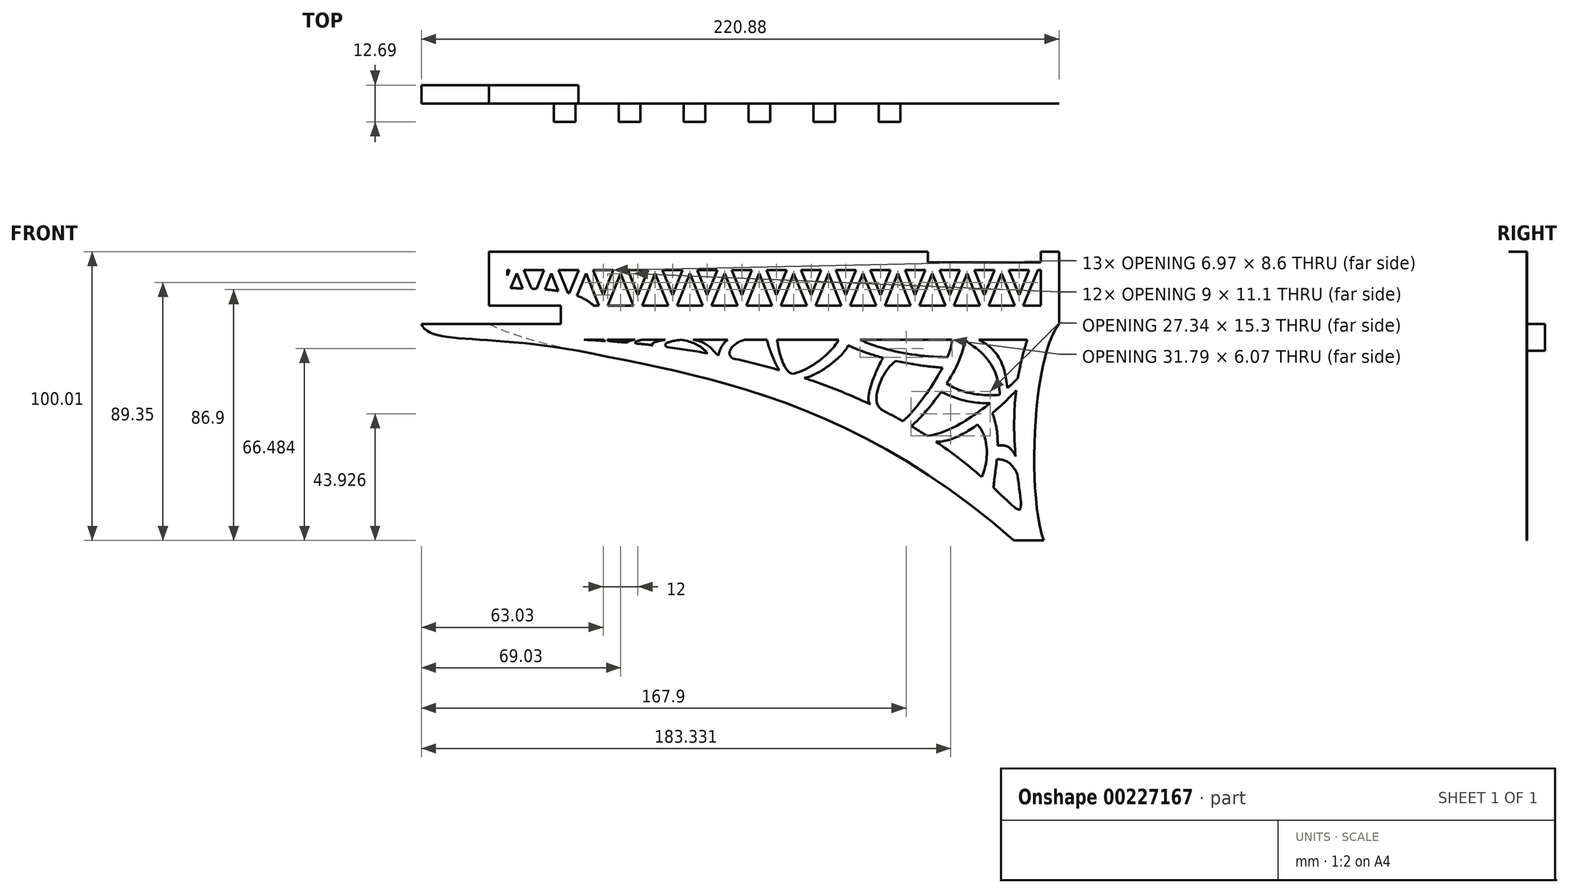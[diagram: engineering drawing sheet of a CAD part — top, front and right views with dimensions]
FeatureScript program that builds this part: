
annotation { "Feature Type Name" : "Feature", "Feature Type Description" : "" }
export const myFeature = defineFeature(function(context is Context, id is Id, definition is map)
    precondition{}
    {
        {
            var Q0;
            Q0=qCreatedBy(makeId("Front.planeOp"),FACE);
            var sketch = newSketch(context, id + "F0", { "sketchPlane" : qUnion([Q0])});
            skLineSegment(sketch, "E0.bottom", {"start": v(98.75, -5) * mm, "end": v(-98.75, -5) * mm});
            skLineSegment(sketch, "E0.top", {"start": v(98.75, 20) * mm, "end": v(-98.75, 20) * mm});
            skLineSegment(sketch, "E0.left", {"start": v(98.75, -5) * mm, "end": v(98.75, 20) * mm});
            skLineSegment(sketch, "E0.right", {"start": v(-98.75, -5) * mm, "end": v(-98.75, 20) * mm});
            skPoint(sketch, "E0.middle", {"position": v(0, 0) * mm});
            skFitSpline(sketch, "E1", {"points": [v(98.75, -5) * mm, v(93.4, -80) * mm], "startDerivative": vector(-27.44, -35.05) * mm, "endDerivative": vector(17.25, -51.42) * mm});
            skLineSegment(sketch, "E2", {"start": v(93.4, -80) * mm, "end": v(83.1, -80) * mm});
            skFitSpline(sketch, "E3", {"points": [v(-98.75, -5) * mm, v(83.1, -80) * mm], "startDerivative": vector(105.32, -51.98) * mm, "endDerivative": vector(225.98, -199.97) * mm});
            skLineSegment(sketch, "E4", {"start": v(-65.76, -10.48) * mm, "end": v(87.75, -10.48) * mm});
            skFitSpline(sketch, "E5", {"points": [v(-65.76, -10.48) * mm, v(85.36, -68.89) * mm, v(87.75, -10.48) * mm], "startDerivative": vector(565.84, -25.35) * mm, "endDerivative": vector(76.27, 228.43) * mm});
            skFitSpline(sketch, "E6", {"points": [v(56.07, -45.75) * mm, v(83.89, -28.03) * mm], "startDerivative": vector(28.17, -2.5) * mm, "endDerivative": vector(10.89, 11.9) * mm});
            skFitSpline(sketch, "E7", {"points": [v(53, -43.72) * mm, v(84.48, -23.78) * mm], "startDerivative": vector(32.82, 2.67) * mm, "endDerivative": vector(17.3, 17.3) * mm});
            skFitSpline(sketch, "E8", {"points": [v(80.84, -27.26) * mm, v(70.98, -10.48) * mm], "startDerivative": vector(-2.04, 19.93) * mm, "endDerivative": vector(-22.58, 10.97) * mm});
            skFitSpline(sketch, "E9", {"points": [v(78.24, -29.58) * mm, v(65.8, -10.48) * mm], "startDerivative": vector(-1.39, 23.06) * mm, "endDerivative": vector(-28.1, 16.92) * mm});
            skFitSpline(sketch, "E10", {"points": [v(65.8, -10.48) * mm, v(47.53, -40.35) * mm], "startDerivative": vector(1.99, -23.82) * mm, "endDerivative": vector(-17.85, -13.78) * mm});
            skFitSpline(sketch, "E11", {"points": [v(44.65, -38.69) * mm, v(61.67, -10.48) * mm], "startDerivative": vector(16.03, 13.18) * mm, "endDerivative": vector(-0.09, 21.32) * mm});
            skFitSpline(sketch, "E12", {"points": [v(60.08, -16.55) * mm, v(29.87, -10.48) * mm], "startDerivative": vector(-38.25, 0.68) * mm, "endDerivative": vector(-20.49, 9.63) * mm});
            skFitSpline(sketch, "E13", {"points": [v(58.36, -20.16) * mm, v(22.4, -10.48) * mm], "startDerivative": vector(-35.97, 2.75) * mm, "endDerivative": vector(-25.01, 16.53) * mm});
            skFitSpline(sketch, "E14", {"points": [v(42.18, -17.79) * mm, v(37.31, -34.77) * mm], "startDerivative": vector(-10.68, -6.67) * mm, "endDerivative": vector(14.47, -11.03) * mm});
            skFitSpline(sketch, "E15", {"points": [v(37.76, -16.72) * mm, v(33.33, -32.82) * mm], "startDerivative": vector(-5.25, -9.39) * mm, "endDerivative": vector(6.74, -7.17) * mm});
            skFitSpline(sketch, "E16", {"points": [v(22.4, -10.48) * mm, v(6.22, -22.3) * mm], "startDerivative": vector(-5.63, -11.87) * mm, "endDerivative": vector(-18.63, -2.94) * mm});
            skFitSpline(sketch, "E17", {"points": [v(25.68, -12.35) * mm, v(10.5, -23.68) * mm], "startDerivative": vector(-3.48, -11.13) * mm, "endDerivative": vector(-14.03, -2) * mm});
            skFitSpline(sketch, "E18", {"points": [v(6.22, -22.3) * mm, v(1.1, -10.48) * mm], "startDerivative": vector(-10.68, 5.46) * mm, "endDerivative": vector(-1.53, 8.83) * mm});
            skFitSpline(sketch, "E19", {"points": [v(-2.49, -10.48) * mm, v(1.88, -21) * mm], "startDerivative": vector(2.88, -9.85) * mm, "endDerivative": vector(4.5, -6.05) * mm});
            skFitSpline(sketch, "E20", {"points": [v(-10.24, -10.48) * mm, v(-14.28, -16.93) * mm], "startDerivative": vector(-13.8, -4.46) * mm, "endDerivative": vector(7.54, -4.85) * mm});
            skFitSpline(sketch, "E21", {"points": [v(-15.96, -10.48) * mm, v(-19.26, -15.9) * mm], "startDerivative": vector(-5.38, -2.77) * mm, "endDerivative": vector(-0.7, -3.9) * mm});
            skFitSpline(sketch, "E22", {"points": [v(-32.12, -10.48) * mm, v(-37.03, -12.98) * mm], "startDerivative": vector(-14.9, -1.57) * mm, "endDerivative": vector(4.86, -2.77) * mm});
            skFitSpline(sketch, "E23", {"points": [v(-37.55, -10.48) * mm, v(-41.88, -12.38) * mm], "startDerivative": vector(-5.93, -0.73) * mm, "endDerivative": vector(4.42, -2.32) * mm});
            skFitSpline(sketch, "E24", {"points": [v(-32.12, -10.48) * mm, v(-23, -15.19) * mm], "startDerivative": vector(17.25, -2.68) * mm, "endDerivative": vector(3.13, -3.72) * mm});
            skFitSpline(sketch, "E25", {"points": [v(-19.26, -15.9) * mm, v(-28.02, -10.48) * mm], "startDerivative": vector(-6.33, 5.02) * mm, "endDerivative": vector(-16.76, 2.48) * mm});
            skFitSpline(sketch, "E26", {"points": [v(-57.31, -10.48) * mm, v(-55.24, -11.1) * mm], "startDerivative": vector(-2.73, -0.64) * mm, "endDerivative": vector(6.17, -0.76) * mm});
            skFitSpline(sketch, "E27", {"points": [v(-58.79, -10.48) * mm, v(-58.33, -10.9) * mm], "startDerivative": vector(-3.78, -0.22) * mm, "endDerivative": vector(1.48, -0.38) * mm});
            skFitSpline(sketch, "E28", {"points": [v(-47.96, -10.48) * mm, v(-50.98, -11.45) * mm], "startDerivative": vector(-5.36, -0.47) * mm, "endDerivative": vector(-1.65, -1.26) * mm});
            skFitSpline(sketch, "E29", {"points": [v(-45.44, -10.48) * mm, v(-47.84, -11.75) * mm], "startDerivative": vector(-6.67, -1.19) * mm, "endDerivative": vector(1.44, -1.22) * mm});
            skFitSpline(sketch, "E30", {"points": [v(70.53, -39.87) * mm, v(71.95, -58) * mm], "startDerivative": vector(13.38, -14.75) * mm, "endDerivative": vector(-6.74, -14.62) * mm});
            skFitSpline(sketch, "E31", {"points": [v(75.63, -35.89) * mm, v(76.05, -61.72) * mm], "startDerivative": vector(10.58, -25.76) * mm, "endDerivative": vector(-2.3, -24.81) * mm});
            skFitSpline(sketch, "E32", {"points": [v(77.51, -47.14) * mm, v(83.68, -50.86) * mm], "startDerivative": vector(10.76, 1.7) * mm, "endDerivative": vector(3.59, -7.85) * mm});
            skFitSpline(sketch, "E33", {"points": [v(77.21, -51.88) * mm, v(84.34, -57.03) * mm], "startDerivative": vector(7.86, 0.06) * mm, "endDerivative": vector(6.37, -13.5) * mm});
            skFitSpline(sketch, "E34", {"points": [v(59.86, -25.57) * mm, v(78.24, -29.58) * mm], "startDerivative": vector(13.5, -9.78) * mm, "endDerivative": vector(20.76, 1.45) * mm});
            skFitSpline(sketch, "E35", {"points": [v(57.95, -28.42) * mm, v(74.87, -32.4) * mm], "startDerivative": vector(12.14, -6.33) * mm, "endDerivative": vector(20.42, 1.15) * mm});
            skLineSegment(sketch, "E36", {"start": v(0, -5) * mm, "end": v(0, 7.5) * mm, "construction": true});
            skLineSegment(sketch, "E37", {"start": v(0, 7.5) * mm, "end": v(0, 20) * mm, "construction": true});
            skLineSegment(sketch, "E38.bottom", {"start": v(92.4, 1.35) * mm, "end": v(-92.4, 1.35) * mm});
            skLineSegment(sketch, "E38.top", {"start": v(92.4, 13.65) * mm, "end": v(-92.4, 13.65) * mm});
            skLineSegment(sketch, "E38.left", {"start": v(92.4, 1.35) * mm, "end": v(92.4, 13.65) * mm});
            skLineSegment(sketch, "E38.right", {"start": v(-92.4, 1.35) * mm, "end": v(-92.4, 13.65) * mm});
            skPoint(sketch, "E38.middle", {"position": v(0, 7.5) * mm});
            skFitSpline(sketch, "E39", {"points": [v(-92.4, 7.35) * mm, v(-62.4, 1.35) * mm], "startDerivative": vector(62.88, 0.86) * mm, "endDerivative": vector(10.76, -9.28) * mm});
            skLineSegment(sketch, "E40", {"start": v(98.75, 16.15) * mm, "end": v(-98.75, 16.15) * mm, "construction": true});
            skLineSegment(sketch, "E41", {"start": v(92.4, 13.65) * mm, "end": v(92.4, 16.15) * mm, "construction": true});
            skLineSegment(sketch, "E42", {"start": v(92.4, 16.15) * mm, "end": v(86.4, 1.35) * mm});
            skLineSegment(sketch, "E43", {"start": v(86.4, 1.35) * mm, "end": v(80.4, 16.15) * mm});
            skLineSegment(sketch, "E44", {"start": v(80.4, 16.15) * mm, "end": v(74.4, 1.35) * mm});
            skLineSegment(sketch, "E45", {"start": v(89.4, 16.15) * mm, "end": v(83.4, 1.35) * mm});
            skLineSegment(sketch, "E46", {"start": v(83.4, 1.35) * mm, "end": v(77.4, 16.15) * mm});
            skLineSegment(sketch, "E47", {"start": v(77.4, 16.15) * mm, "end": v(71.4, 1.35) * mm});
            skLineSegment(sketch, "E48.1.0.0", {"start": v(65.4, 16.15) * mm, "end": v(59.4, 1.35) * mm});
            skLineSegment(sketch, "E48.1.0.1", {"start": v(68.4, 16.15) * mm, "end": v(62.4, 1.35) * mm});
            skLineSegment(sketch, "E48.1.0.2", {"start": v(71.4, 1.35) * mm, "end": v(65.4, 16.15) * mm});
            skLineSegment(sketch, "E48.1.0.3", {"start": v(74.4, 1.35) * mm, "end": v(68.4, 16.15) * mm});
            skLineSegment(sketch, "E48.2.0.0", {"start": v(53.4, 16.15) * mm, "end": v(47.4, 1.35) * mm});
            skLineSegment(sketch, "E48.2.0.1", {"start": v(56.4, 16.15) * mm, "end": v(50.4, 1.35) * mm});
            skLineSegment(sketch, "E48.2.0.2", {"start": v(59.4, 1.35) * mm, "end": v(53.4, 16.15) * mm});
            skLineSegment(sketch, "E48.2.0.3", {"start": v(62.4, 1.35) * mm, "end": v(56.4, 16.15) * mm});
            skLineSegment(sketch, "E48.3.0.0", {"start": v(41.4, 16.15) * mm, "end": v(35.4, 1.35) * mm});
            skLineSegment(sketch, "E48.3.0.1", {"start": v(44.4, 16.15) * mm, "end": v(38.4, 1.35) * mm});
            skLineSegment(sketch, "E48.3.0.2", {"start": v(47.4, 1.35) * mm, "end": v(41.4, 16.15) * mm});
            skLineSegment(sketch, "E48.3.0.3", {"start": v(50.4, 1.35) * mm, "end": v(44.4, 16.15) * mm});
            skLineSegment(sketch, "E48.4.0.0", {"start": v(29.4, 16.15) * mm, "end": v(23.4, 1.35) * mm});
            skLineSegment(sketch, "E48.4.0.1", {"start": v(32.4, 16.15) * mm, "end": v(26.4, 1.35) * mm});
            skLineSegment(sketch, "E48.4.0.2", {"start": v(35.4, 1.35) * mm, "end": v(29.4, 16.15) * mm});
            skLineSegment(sketch, "E48.4.0.3", {"start": v(38.4, 1.35) * mm, "end": v(32.4, 16.15) * mm});
            skLineSegment(sketch, "E48.5.0.0", {"start": v(17.4, 16.15) * mm, "end": v(11.4, 1.35) * mm});
            skLineSegment(sketch, "E48.5.0.1", {"start": v(20.4, 16.15) * mm, "end": v(14.4, 1.35) * mm});
            skLineSegment(sketch, "E48.5.0.2", {"start": v(23.4, 1.35) * mm, "end": v(17.4, 16.15) * mm});
            skLineSegment(sketch, "E48.5.0.3", {"start": v(26.4, 1.35) * mm, "end": v(20.4, 16.15) * mm});
            skLineSegment(sketch, "E48.6.0.0", {"start": v(5.4, 16.15) * mm, "end": v(-0.6, 1.35) * mm});
            skLineSegment(sketch, "E48.6.0.1", {"start": v(8.4, 16.15) * mm, "end": v(2.4, 1.35) * mm});
            skLineSegment(sketch, "E48.6.0.2", {"start": v(11.4, 1.35) * mm, "end": v(5.4, 16.15) * mm});
            skLineSegment(sketch, "E48.6.0.3", {"start": v(14.4, 1.35) * mm, "end": v(8.4, 16.15) * mm});
            skLineSegment(sketch, "E48.7.0.0", {"start": v(-6.6, 16.15) * mm, "end": v(-12.6, 1.35) * mm});
            skLineSegment(sketch, "E48.7.0.1", {"start": v(-3.6, 16.15) * mm, "end": v(-9.6, 1.35) * mm});
            skLineSegment(sketch, "E48.7.0.2", {"start": v(-0.6, 1.35) * mm, "end": v(-6.6, 16.15) * mm});
            skLineSegment(sketch, "E48.7.0.3", {"start": v(2.4, 1.35) * mm, "end": v(-3.6, 16.15) * mm});
            skLineSegment(sketch, "E48.8.0.0", {"start": v(-18.6, 16.15) * mm, "end": v(-24.6, 1.35) * mm});
            skLineSegment(sketch, "E48.8.0.1", {"start": v(-15.6, 16.15) * mm, "end": v(-21.6, 1.35) * mm});
            skLineSegment(sketch, "E48.8.0.2", {"start": v(-12.6, 1.35) * mm, "end": v(-18.6, 16.15) * mm});
            skLineSegment(sketch, "E48.8.0.3", {"start": v(-9.6, 1.35) * mm, "end": v(-15.6, 16.15) * mm});
            skLineSegment(sketch, "E48.9.0.0", {"start": v(-30.6, 16.15) * mm, "end": v(-36.6, 1.35) * mm});
            skLineSegment(sketch, "E48.9.0.1", {"start": v(-27.6, 16.15) * mm, "end": v(-33.6, 1.35) * mm});
            skLineSegment(sketch, "E48.9.0.2", {"start": v(-24.6, 1.35) * mm, "end": v(-30.6, 16.15) * mm});
            skLineSegment(sketch, "E48.9.0.3", {"start": v(-21.6, 1.35) * mm, "end": v(-27.6, 16.15) * mm});
            skLineSegment(sketch, "E48.10.0.0", {"start": v(-42.6, 16.15) * mm, "end": v(-48.6, 1.35) * mm});
            skLineSegment(sketch, "E48.10.0.1", {"start": v(-39.6, 16.15) * mm, "end": v(-45.6, 1.35) * mm});
            skLineSegment(sketch, "E48.10.0.2", {"start": v(-36.6, 1.35) * mm, "end": v(-42.6, 16.15) * mm});
            skLineSegment(sketch, "E48.10.0.3", {"start": v(-33.6, 1.35) * mm, "end": v(-39.6, 16.15) * mm});
            skLineSegment(sketch, "E48.11.0.0", {"start": v(-54.6, 16.15) * mm, "end": v(-60.6, 1.35) * mm});
            skLineSegment(sketch, "E48.11.0.1", {"start": v(-51.6, 16.15) * mm, "end": v(-57.6, 1.35) * mm});
            skLineSegment(sketch, "E48.11.0.2", {"start": v(-48.6, 1.35) * mm, "end": v(-54.6, 16.15) * mm});
            skLineSegment(sketch, "E48.11.0.3", {"start": v(-45.6, 1.35) * mm, "end": v(-51.6, 16.15) * mm});
            skLineSegment(sketch, "E48.12.0.0", {"start": v(-66.6, 16.15) * mm, "end": v(-72.6, 1.35) * mm});
            skLineSegment(sketch, "E48.12.0.1", {"start": v(-63.6, 16.15) * mm, "end": v(-69.6, 1.35) * mm});
            skLineSegment(sketch, "E48.12.0.2", {"start": v(-60.6, 1.35) * mm, "end": v(-66.6, 16.15) * mm});
            skLineSegment(sketch, "E48.12.0.3", {"start": v(-57.6, 1.35) * mm, "end": v(-63.6, 16.15) * mm});
            skLineSegment(sketch, "E48.13.0.0", {"start": v(-78.6, 16.15) * mm, "end": v(-84.6, 1.35) * mm});
            skLineSegment(sketch, "E48.13.0.1", {"start": v(-75.6, 16.15) * mm, "end": v(-81.6, 1.35) * mm});
            skLineSegment(sketch, "E48.13.0.2", {"start": v(-72.6, 1.35) * mm, "end": v(-78.6, 16.15) * mm});
            skLineSegment(sketch, "E48.13.0.3", {"start": v(-69.6, 1.35) * mm, "end": v(-75.6, 16.15) * mm});
            skLineSegment(sketch, "E48.14.0.0", {"start": v(-90.6, 16.15) * mm, "end": v(-96.6, 1.35) * mm});
            skLineSegment(sketch, "E48.14.0.1", {"start": v(-87.6, 16.15) * mm, "end": v(-93.6, 1.35) * mm});
            skLineSegment(sketch, "E48.14.0.2", {"start": v(-84.6, 1.35) * mm, "end": v(-90.6, 16.15) * mm});
            skLineSegment(sketch, "E48.14.0.3", {"start": v(-81.6, 1.35) * mm, "end": v(-87.6, 16.15) * mm});
            skLineSegment(sketch, "E48.direction1", {"start": v(71.4, 1.35) * mm, "end": v(59.4, 1.35) * mm, "construction": true});
            skSolve(sketch);
        }
        {
            var Q0;
            Q0=makeQuery(id+"F0.imprint","IMPRINT",FACE,{"disambiguationData":[TD([[makeQuery(id+"F0.imprint","IMPRINT",EDGE,{"derivedFrom":sQuery(id+"F0.wireOp",EDGE,"E0.bottom")}),1.0]])]});
            var Q1;
            {var subQ0=sQuery(id+"F0.wireOp",EDGE,"E8");Q1=makeQuery(id+"F0.imprint","IMPRINT",FACE,{"disambiguationData":[TD([[makeQuery(id+"F0.imprint","IMPRINT",EDGE,{"derivedFrom":subQ0}),1.0]])]});}
            var Q2;
            {var subQ4=sQuery(id+"F0.wireOp",EDGE,"E6");Q2=makeQuery(id+"F0.imprint","IMPRINT",FACE,{"disambiguationData":[TD([[makeQuery(id+"F0.imprint","IMPRINT",EDGE,{"derivedFrom":subQ4}),1.0]])]});}
            var Q3;
            {var subQ4=sQuery(id+"F0.wireOp",EDGE,"E12");Q3=makeQuery(id+"F0.imprint","IMPRINT",FACE,{"disambiguationData":[TD([[makeQuery(id+"F0.imprint","IMPRINT",EDGE,{"derivedFrom":subQ4}),1.0]])]});}
            var Q4;
            {var subQ4=sQuery(id+"F0.wireOp",EDGE,"E10");Q4=makeQuery(id+"F0.imprint","IMPRINT",FACE,{"disambiguationData":[TD([[makeQuery(id+"F0.imprint","IMPRINT",EDGE,{"derivedFrom":subQ4}),-1.0]])]});}
            var Q5;
            {var subQ0=sQuery(id+"F0.wireOp",EDGE,"E14");Q5=makeQuery(id+"F0.imprint","IMPRINT",FACE,{"disambiguationData":[TD([[makeQuery(id+"F0.imprint","IMPRINT",EDGE,{"derivedFrom":subQ0}),-1.0]])]});}
            var Q6;
            {var subQ0=sQuery(id+"F0.wireOp",EDGE,"E18");Q6=makeQuery(id+"F0.imprint","IMPRINT",FACE,{"disambiguationData":[TD([[makeQuery(id+"F0.imprint","IMPRINT",EDGE,{"derivedFrom":subQ0}),1.0]])]});}
            var Q7;
            {var subQ0=sQuery(id+"F0.wireOp",EDGE,"E20");Q7=makeQuery(id+"F0.imprint","IMPRINT",FACE,{"disambiguationData":[TD([[makeQuery(id+"F0.imprint","IMPRINT",EDGE,{"derivedFrom":subQ0}),-1.0]])]});}
            var Q8;
            {var subQ0=sQuery(id+"F0.wireOp",EDGE,"E16");Q8=makeQuery(id+"F0.imprint","IMPRINT",FACE,{"disambiguationData":[TD([[makeQuery(id+"F0.imprint","IMPRINT",EDGE,{"derivedFrom":subQ0}),1.0]])]});}
            var Q9;
            {var subQ0=sQuery(id+"F0.wireOp",EDGE,"E22");Q9=makeQuery(id+"F0.imprint","IMPRINT",FACE,{"disambiguationData":[TD([[makeQuery(id+"F0.imprint","IMPRINT",EDGE,{"derivedFrom":subQ0}),-1.0]])]});}
            var Q10;
            {var subQ0=sQuery(id+"F0.wireOp",EDGE,"E24");Q10=makeQuery(id+"F0.imprint","IMPRINT",FACE,{"disambiguationData":[TD([[makeQuery(id+"F0.imprint","IMPRINT",EDGE,{"derivedFrom":subQ0}),1.0]])]});}
            var Q11;
            {var subQ3=sQuery(id+"F0.wireOp",EDGE,"E26");Q11=makeQuery(id+"F0.imprint","IMPRINT",FACE,{"disambiguationData":[TD([[makeQuery(id+"F0.imprint","IMPRINT",EDGE,{"derivedFrom":subQ3}),-1.0]])]});}
            var Q12;
            {var subQ0=sQuery(id+"F0.wireOp",EDGE,"E28");Q12=makeQuery(id+"F0.imprint","IMPRINT",FACE,{"disambiguationData":[TD([[makeQuery(id+"F0.imprint","IMPRINT",EDGE,{"derivedFrom":subQ0}),1.0]])]});}
            var Q13;
            {var subQ0=sQuery(id+"F0.wireOp",EDGE,"0f1a2a49-f85b-4a7b-b702-23d574d83e41");Q13=makeQuery(id+"F0.imprint","IMPRINT",FACE,{"disambiguationData":[TD([[makeQuery(id+"F0.imprint","IMPRINT",EDGE,{"derivedFrom":subQ0}),-1.0]])]});}
            var Q14;
            {var subQ0=sQuery(id+"F0.wireOp",EDGE,"ffe359e4-6994-4db7-aa5d-63739de77c5f");Q14=makeQuery(id+"F0.imprint","IMPRINT",FACE,{"disambiguationData":[TD([[makeQuery(id+"F0.imprint","IMPRINT",EDGE,{"derivedFrom":subQ0}),-1.0]])]});}
            var Q15;
            {var subQ4=sQuery(id+"F0.wireOp",EDGE,"E30");Q15=makeQuery(id+"F0.imprint","IMPRINT",FACE,{"disambiguationData":[TD([[makeQuery(id+"F0.imprint","IMPRINT",EDGE,{"derivedFrom":subQ4}),1.0]])]});}
            var Q16;
            {var subQ0=sQuery(id+"F0.wireOp",EDGE,"E32");Q16=makeQuery(id+"F0.imprint","IMPRINT",FACE,{"disambiguationData":[TD([[makeQuery(id+"F0.imprint","IMPRINT",EDGE,{"derivedFrom":subQ0}),-1.0]])]});}
            var Q17;
            {var subQ0=sQuery(id+"F0.wireOp",EDGE,"E34");Q17=makeQuery(id+"F0.imprint","IMPRINT",FACE,{"disambiguationData":[TD([[makeQuery(id+"F0.imprint","IMPRINT",EDGE,{"derivedFrom":subQ0}),-1.0]])]});}
            var Q18;
            {var subQ0=sQuery(id+"F0.wireOp",EDGE,"GfOTP1Av-60BQ-FTfT-Dyfk-SZfRFgkm87CM");Q18=makeQuery(id+"F0.imprint","IMPRINT",FACE,{"disambiguationData":[TD([[makeQuery(id+"F0.imprint","IMPRINT",EDGE,{"derivedFrom":subQ0}),1.0]])]});}
            var Q19;
            {var subQ3=sQuery(id+"F0.wireOp",EDGE,"E39");Q19=makeQuery(id+"F0.imprint","IMPRINT",FACE,{"disambiguationData":[TD([[makeQuery(id+"F0.imprint","IMPRINT",EDGE,{"derivedFrom":subQ3}),-1.0]])]});}
            var Q20;
            {var subQ0=sQuery(id+"F0.wireOp",EDGE,"6nG8yHqI-1RSW-Lih2-RL7p-Ogt5qLZxJ40G");Q20=makeQuery(id+"F0.imprint","IMPRINT",FACE,{"disambiguationData":[TD([[makeQuery(id+"F0.imprint","IMPRINT",EDGE,{"derivedFrom":subQ0}),-1.0]])]});}
            var Q21;
            {var subQ0=sQuery(id+"F0.wireOp",EDGE,"vsQBDWpD-XZvz-YL4w-sYMF-8ExcL3MSyagj");var subQ3=sQuery(id+"F0.wireOp",EDGE,"ahGiBcFi-U1tk-ofgL-IaMi-E3z2y5cFStP9");var subQ5=makeQuery(id+"F0.imprint","INTERSECT",VERTEX,{"derivedFrom":[subQ0,subQ3]});Q21=makeQuery(id+"F0.imprint","IMPRINT",FACE,{"disambiguationData":[TD([[makeQuery(id+"F0.imprint","IMPRINT",EDGE,{"disambiguationData":[TD([[subQ5,-1.0]])],"derivedFrom":subQ0}),1.0]])]});}
            var Q22;
            {var subQ0=sQuery(id+"F0.wireOp",EDGE,"E46");var subQ1=sQuery(id+"F0.wireOp",EDGE,"E38.top");var subQ2=makeQuery(id+"F0.imprint","INTERSECT",VERTEX,{"derivedFrom":[subQ1,subQ0]});Q22=makeQuery(id+"F0.imprint","IMPRINT",FACE,{"disambiguationData":[TD([[makeQuery(id+"F0.imprint","IMPRINT",EDGE,{"disambiguationData":[TD([[subQ2,-1.0]])],"derivedFrom":subQ1}),-1.0]])]});}
            var Q23;
            {var subQ0=sQuery(id+"F0.wireOp",EDGE,"E43");var subQ1=sQuery(id+"F0.wireOp",EDGE,"E38.top");var subQ2=makeQuery(id+"F0.imprint","INTERSECT",VERTEX,{"derivedFrom":[subQ1,subQ0]});Q23=makeQuery(id+"F0.imprint","IMPRINT",FACE,{"disambiguationData":[TD([[makeQuery(id+"F0.imprint","IMPRINT",EDGE,{"disambiguationData":[TD([[subQ2,-1.0]])],"derivedFrom":subQ1}),-1.0]])]});}
            var Q24;
            {var subQ1=sQuery(id+"F0.wireOp",EDGE,"E38.right");var subQ7=sQuery(id+"F0.wireOp",EDGE,"E38.bottom");var subQ8=makeQuery(id+"F0.imprint","INTERSECT",VERTEX,{"derivedFrom":[subQ7,subQ1]});Q24=makeQuery(id+"F0.imprint","IMPRINT",FACE,{"disambiguationData":[TD([[makeQuery(id+"F0.imprint","IMPRINT",EDGE,{"disambiguationData":[TD([[subQ8,-1.0]])],"derivedFrom":subQ1}),-1.0]])]});}
            var Q25;
            {var subQ0=sQuery(id+"F0.wireOp",EDGE,"E48.14.0.2");var subQ1=sQuery(id+"F0.wireOp",EDGE,"E39");var subQ2=makeQuery(id+"F0.imprint","INTERSECT",VERTEX,{"derivedFrom":[subQ1,subQ0]});Q25=makeQuery(id+"F0.imprint","IMPRINT",FACE,{"disambiguationData":[TD([[makeQuery(id+"F0.imprint","IMPRINT",EDGE,{"disambiguationData":[TD([[subQ2,-1.0]])],"derivedFrom":subQ1}),-1.0]])]});}
            var Q26;
            {var subQ0=sQuery(id+"F0.wireOp",EDGE,"E48.13.0.0");var subQ3=sQuery(id+"F0.wireOp",EDGE,"E48.14.0.3");var subQ5=makeQuery(id+"F0.imprint","INTERSECT",VERTEX,{"derivedFrom":[subQ0,subQ3]});Q26=makeQuery(id+"F0.imprint","IMPRINT",FACE,{"disambiguationData":[TD([[makeQuery(id+"F0.imprint","IMPRINT",EDGE,{"disambiguationData":[TD([[subQ5,-1.0]])],"derivedFrom":subQ0}),1.0]])]});}
            var Q27;
            {var subQ0=sQuery(id+"F0.wireOp",EDGE,"E48.13.0.0");var subQ1=sQuery(id+"F0.wireOp",EDGE,"E39");var subQ2=makeQuery(id+"F0.imprint","INTERSECT",VERTEX,{"derivedFrom":[subQ1,subQ0]});Q27=makeQuery(id+"F0.imprint","IMPRINT",FACE,{"disambiguationData":[TD([[makeQuery(id+"F0.imprint","IMPRINT",EDGE,{"disambiguationData":[TD([[subQ2,-1.0]])],"derivedFrom":subQ1}),-1.0]])]});}
            var Q28;
            {var subQ3=sQuery(id+"F0.wireOp",EDGE,"E48.13.0.1");var subQ5=sQuery(id+"F0.wireOp",EDGE,"E39");var subQ6=makeQuery(id+"F0.imprint","INTERSECT",VERTEX,{"derivedFrom":[subQ5,subQ3]});Q28=makeQuery(id+"F0.imprint","IMPRINT",FACE,{"disambiguationData":[TD([[makeQuery(id+"F0.imprint","IMPRINT",EDGE,{"disambiguationData":[TD([[subQ6,-1.0]])],"derivedFrom":subQ5}),-1.0]])]});}
            var Q29;
            {var subQ0=sQuery(id+"F0.wireOp",EDGE,"E48.13.0.2");var subQ1=sQuery(id+"F0.wireOp",EDGE,"E39");var subQ2=makeQuery(id+"F0.imprint","INTERSECT",VERTEX,{"derivedFrom":[subQ1,subQ0]});Q29=makeQuery(id+"F0.imprint","IMPRINT",FACE,{"disambiguationData":[TD([[makeQuery(id+"F0.imprint","IMPRINT",EDGE,{"disambiguationData":[TD([[subQ2,-1.0]])],"derivedFrom":subQ1}),-1.0]])]});}
            var Q30;
            {var subQ0=sQuery(id+"F0.wireOp",EDGE,"E48.12.0.0");var subQ3=sQuery(id+"F0.wireOp",EDGE,"E48.13.0.3");var subQ5=makeQuery(id+"F0.imprint","INTERSECT",VERTEX,{"derivedFrom":[subQ0,subQ3]});Q30=makeQuery(id+"F0.imprint","IMPRINT",FACE,{"disambiguationData":[TD([[makeQuery(id+"F0.imprint","IMPRINT",EDGE,{"disambiguationData":[TD([[subQ5,-1.0]])],"derivedFrom":subQ0}),1.0]])]});}
            var Q31;
            {var subQ0=sQuery(id+"F0.wireOp",EDGE,"E48.12.0.0");var subQ1=sQuery(id+"F0.wireOp",EDGE,"E39");var subQ2=makeQuery(id+"F0.imprint","INTERSECT",VERTEX,{"derivedFrom":[subQ1,subQ0]});Q31=makeQuery(id+"F0.imprint","IMPRINT",FACE,{"disambiguationData":[TD([[makeQuery(id+"F0.imprint","IMPRINT",EDGE,{"disambiguationData":[TD([[subQ2,-1.0]])],"derivedFrom":subQ1}),-1.0]])]});}
            var Q32;
            {var subQ0=sQuery(id+"F0.wireOp",EDGE,"E48.14.0.3");var subQ1=sQuery(id+"F0.wireOp",EDGE,"E38.top");var subQ2=makeQuery(id+"F0.imprint","INTERSECT",VERTEX,{"derivedFrom":[subQ1,subQ0]});Q32=makeQuery(id+"F0.imprint","IMPRINT",FACE,{"disambiguationData":[TD([[makeQuery(id+"F0.imprint","IMPRINT",EDGE,{"disambiguationData":[TD([[subQ2,-1.0]])],"derivedFrom":subQ1}),-1.0]])]});}
            var Q33;
            {var subQ0=sQuery(id+"F0.wireOp",EDGE,"E48.14.0.2");var subQ1=sQuery(id+"F0.wireOp",EDGE,"E38.top");var subQ2=makeQuery(id+"F0.imprint","INTERSECT",VERTEX,{"derivedFrom":[subQ1,subQ0]});Q33=makeQuery(id+"F0.imprint","IMPRINT",FACE,{"disambiguationData":[TD([[makeQuery(id+"F0.imprint","IMPRINT",EDGE,{"disambiguationData":[TD([[subQ2,-1.0]])],"derivedFrom":subQ1}),-1.0]])]});}
            var Q34;
            {var subQ0=sQuery(id+"F0.wireOp",EDGE,"E48.13.0.2");var subQ1=sQuery(id+"F0.wireOp",EDGE,"E38.top");var subQ2=makeQuery(id+"F0.imprint","INTERSECT",VERTEX,{"derivedFrom":[subQ1,subQ0]});Q34=makeQuery(id+"F0.imprint","IMPRINT",FACE,{"disambiguationData":[TD([[makeQuery(id+"F0.imprint","IMPRINT",EDGE,{"disambiguationData":[TD([[subQ2,-1.0]])],"derivedFrom":subQ1}),-1.0]])]});}
            var Q35;
            {var subQ0=sQuery(id+"F0.wireOp",EDGE,"E48.13.0.3");var subQ1=sQuery(id+"F0.wireOp",EDGE,"E38.top");var subQ2=makeQuery(id+"F0.imprint","INTERSECT",VERTEX,{"derivedFrom":[subQ1,subQ0]});Q35=makeQuery(id+"F0.imprint","IMPRINT",FACE,{"disambiguationData":[TD([[makeQuery(id+"F0.imprint","IMPRINT",EDGE,{"disambiguationData":[TD([[subQ2,-1.0]])],"derivedFrom":subQ1}),-1.0]])]});}
            var Q36;
            {var subQ0=sQuery(id+"F0.wireOp",EDGE,"E48.12.0.2");var subQ1=sQuery(id+"F0.wireOp",EDGE,"E38.top");var subQ2=makeQuery(id+"F0.imprint","INTERSECT",VERTEX,{"derivedFrom":[subQ1,subQ0]});Q36=makeQuery(id+"F0.imprint","IMPRINT",FACE,{"disambiguationData":[TD([[makeQuery(id+"F0.imprint","IMPRINT",EDGE,{"disambiguationData":[TD([[subQ2,-1.0]])],"derivedFrom":subQ1}),-1.0]])]});}
            var Q37;
            {var subQ0=sQuery(id+"F0.wireOp",EDGE,"E48.12.0.3");var subQ1=sQuery(id+"F0.wireOp",EDGE,"E38.top");var subQ2=makeQuery(id+"F0.imprint","INTERSECT",VERTEX,{"derivedFrom":[subQ1,subQ0]});Q37=makeQuery(id+"F0.imprint","IMPRINT",FACE,{"disambiguationData":[TD([[makeQuery(id+"F0.imprint","IMPRINT",EDGE,{"disambiguationData":[TD([[subQ2,-1.0]])],"derivedFrom":subQ1}),-1.0]])]});}
            var Q38;
            {var subQ0=sQuery(id+"F0.wireOp",EDGE,"E48.11.0.2");var subQ1=sQuery(id+"F0.wireOp",EDGE,"E38.top");var subQ2=makeQuery(id+"F0.imprint","INTERSECT",VERTEX,{"derivedFrom":[subQ1,subQ0]});Q38=makeQuery(id+"F0.imprint","IMPRINT",FACE,{"disambiguationData":[TD([[makeQuery(id+"F0.imprint","IMPRINT",EDGE,{"disambiguationData":[TD([[subQ2,-1.0]])],"derivedFrom":subQ1}),-1.0]])]});}
            var Q39;
            {var subQ0=sQuery(id+"F0.wireOp",EDGE,"E48.11.0.3");var subQ1=sQuery(id+"F0.wireOp",EDGE,"E38.top");var subQ2=makeQuery(id+"F0.imprint","INTERSECT",VERTEX,{"derivedFrom":[subQ1,subQ0]});Q39=makeQuery(id+"F0.imprint","IMPRINT",FACE,{"disambiguationData":[TD([[makeQuery(id+"F0.imprint","IMPRINT",EDGE,{"disambiguationData":[TD([[subQ2,-1.0]])],"derivedFrom":subQ1}),-1.0]])]});}
            var Q40;
            {var subQ0=sQuery(id+"F0.wireOp",EDGE,"E48.10.0.2");var subQ1=sQuery(id+"F0.wireOp",EDGE,"E38.top");var subQ2=makeQuery(id+"F0.imprint","INTERSECT",VERTEX,{"derivedFrom":[subQ1,subQ0]});Q40=makeQuery(id+"F0.imprint","IMPRINT",FACE,{"disambiguationData":[TD([[makeQuery(id+"F0.imprint","IMPRINT",EDGE,{"disambiguationData":[TD([[subQ2,-1.0]])],"derivedFrom":subQ1}),-1.0]])]});}
            var Q41;
            {var subQ0=sQuery(id+"F0.wireOp",EDGE,"E48.10.0.3");var subQ1=sQuery(id+"F0.wireOp",EDGE,"E38.top");var subQ2=makeQuery(id+"F0.imprint","INTERSECT",VERTEX,{"derivedFrom":[subQ1,subQ0]});Q41=makeQuery(id+"F0.imprint","IMPRINT",FACE,{"disambiguationData":[TD([[makeQuery(id+"F0.imprint","IMPRINT",EDGE,{"disambiguationData":[TD([[subQ2,-1.0]])],"derivedFrom":subQ1}),-1.0]])]});}
            var Q42;
            {var subQ0=sQuery(id+"F0.wireOp",EDGE,"E48.9.0.2");var subQ1=sQuery(id+"F0.wireOp",EDGE,"E38.top");var subQ2=makeQuery(id+"F0.imprint","INTERSECT",VERTEX,{"derivedFrom":[subQ1,subQ0]});Q42=makeQuery(id+"F0.imprint","IMPRINT",FACE,{"disambiguationData":[TD([[makeQuery(id+"F0.imprint","IMPRINT",EDGE,{"disambiguationData":[TD([[subQ2,-1.0]])],"derivedFrom":subQ1}),-1.0]])]});}
            var Q43;
            {var subQ0=sQuery(id+"F0.wireOp",EDGE,"E48.9.0.3");var subQ1=sQuery(id+"F0.wireOp",EDGE,"E38.top");var subQ2=makeQuery(id+"F0.imprint","INTERSECT",VERTEX,{"derivedFrom":[subQ1,subQ0]});Q43=makeQuery(id+"F0.imprint","IMPRINT",FACE,{"disambiguationData":[TD([[makeQuery(id+"F0.imprint","IMPRINT",EDGE,{"disambiguationData":[TD([[subQ2,-1.0]])],"derivedFrom":subQ1}),-1.0]])]});}
            var Q44;
            {var subQ0=sQuery(id+"F0.wireOp",EDGE,"E48.8.0.2");var subQ1=sQuery(id+"F0.wireOp",EDGE,"E38.top");var subQ2=makeQuery(id+"F0.imprint","INTERSECT",VERTEX,{"derivedFrom":[subQ1,subQ0]});Q44=makeQuery(id+"F0.imprint","IMPRINT",FACE,{"disambiguationData":[TD([[makeQuery(id+"F0.imprint","IMPRINT",EDGE,{"disambiguationData":[TD([[subQ2,-1.0]])],"derivedFrom":subQ1}),-1.0]])]});}
            var Q45;
            {var subQ0=sQuery(id+"F0.wireOp",EDGE,"E48.8.0.3");var subQ1=sQuery(id+"F0.wireOp",EDGE,"E38.top");var subQ2=makeQuery(id+"F0.imprint","INTERSECT",VERTEX,{"derivedFrom":[subQ1,subQ0]});Q45=makeQuery(id+"F0.imprint","IMPRINT",FACE,{"disambiguationData":[TD([[makeQuery(id+"F0.imprint","IMPRINT",EDGE,{"disambiguationData":[TD([[subQ2,-1.0]])],"derivedFrom":subQ1}),-1.0]])]});}
            var Q46;
            {var subQ0=sQuery(id+"F0.wireOp",EDGE,"E48.7.0.2");var subQ1=sQuery(id+"F0.wireOp",EDGE,"E38.top");var subQ2=makeQuery(id+"F0.imprint","INTERSECT",VERTEX,{"derivedFrom":[subQ1,subQ0]});Q46=makeQuery(id+"F0.imprint","IMPRINT",FACE,{"disambiguationData":[TD([[makeQuery(id+"F0.imprint","IMPRINT",EDGE,{"disambiguationData":[TD([[subQ2,-1.0]])],"derivedFrom":subQ1}),-1.0]])]});}
            var Q47;
            {var subQ0=sQuery(id+"F0.wireOp",EDGE,"E48.7.0.3");var subQ1=sQuery(id+"F0.wireOp",EDGE,"E38.top");var subQ2=makeQuery(id+"F0.imprint","INTERSECT",VERTEX,{"derivedFrom":[subQ1,subQ0]});Q47=makeQuery(id+"F0.imprint","IMPRINT",FACE,{"disambiguationData":[TD([[makeQuery(id+"F0.imprint","IMPRINT",EDGE,{"disambiguationData":[TD([[subQ2,-1.0]])],"derivedFrom":subQ1}),-1.0]])]});}
            var Q48;
            {var subQ0=sQuery(id+"F0.wireOp",EDGE,"E48.6.0.2");var subQ1=sQuery(id+"F0.wireOp",EDGE,"E38.top");var subQ2=makeQuery(id+"F0.imprint","INTERSECT",VERTEX,{"derivedFrom":[subQ1,subQ0]});Q48=makeQuery(id+"F0.imprint","IMPRINT",FACE,{"disambiguationData":[TD([[makeQuery(id+"F0.imprint","IMPRINT",EDGE,{"disambiguationData":[TD([[subQ2,-1.0]])],"derivedFrom":subQ1}),-1.0]])]});}
            var Q49;
            {var subQ0=sQuery(id+"F0.wireOp",EDGE,"E48.6.0.3");var subQ1=sQuery(id+"F0.wireOp",EDGE,"E38.top");var subQ2=makeQuery(id+"F0.imprint","INTERSECT",VERTEX,{"derivedFrom":[subQ1,subQ0]});Q49=makeQuery(id+"F0.imprint","IMPRINT",FACE,{"disambiguationData":[TD([[makeQuery(id+"F0.imprint","IMPRINT",EDGE,{"disambiguationData":[TD([[subQ2,-1.0]])],"derivedFrom":subQ1}),-1.0]])]});}
            var Q50;
            {var subQ0=sQuery(id+"F0.wireOp",EDGE,"E48.5.0.2");var subQ1=sQuery(id+"F0.wireOp",EDGE,"E38.top");var subQ2=makeQuery(id+"F0.imprint","INTERSECT",VERTEX,{"derivedFrom":[subQ1,subQ0]});Q50=makeQuery(id+"F0.imprint","IMPRINT",FACE,{"disambiguationData":[TD([[makeQuery(id+"F0.imprint","IMPRINT",EDGE,{"disambiguationData":[TD([[subQ2,-1.0]])],"derivedFrom":subQ1}),-1.0]])]});}
            var Q51;
            Q51=makeQuery(id+"F0.imprint","IMPRINT",FACE,{"disambiguationData":[TD([[makeQuery(id+"F0.imprint","IMPRINT",EDGE,{"derivedFrom":sQuery(id+"F0.wireOp",EDGE,"E0.bottom")}),-1.0]])]});
            var Q52;
            {var subQ0=sQuery(id+"F0.wireOp",EDGE,"E48.5.0.3");var subQ1=sQuery(id+"F0.wireOp",EDGE,"E38.top");var subQ2=makeQuery(id+"F0.imprint","INTERSECT",VERTEX,{"derivedFrom":[subQ1,subQ0]});Q52=makeQuery(id+"F0.imprint","IMPRINT",FACE,{"disambiguationData":[TD([[makeQuery(id+"F0.imprint","IMPRINT",EDGE,{"disambiguationData":[TD([[subQ2,-1.0]])],"derivedFrom":subQ1}),-1.0]])]});}
            var Q53;
            {var subQ0=sQuery(id+"F0.wireOp",EDGE,"E48.4.0.2");var subQ1=sQuery(id+"F0.wireOp",EDGE,"E38.top");var subQ2=makeQuery(id+"F0.imprint","INTERSECT",VERTEX,{"derivedFrom":[subQ1,subQ0]});Q53=makeQuery(id+"F0.imprint","IMPRINT",FACE,{"disambiguationData":[TD([[makeQuery(id+"F0.imprint","IMPRINT",EDGE,{"disambiguationData":[TD([[subQ2,-1.0]])],"derivedFrom":subQ1}),-1.0]])]});}
            var Q54;
            {var subQ0=sQuery(id+"F0.wireOp",EDGE,"E48.4.0.3");var subQ1=sQuery(id+"F0.wireOp",EDGE,"E38.top");var subQ2=makeQuery(id+"F0.imprint","INTERSECT",VERTEX,{"derivedFrom":[subQ1,subQ0]});Q54=makeQuery(id+"F0.imprint","IMPRINT",FACE,{"disambiguationData":[TD([[makeQuery(id+"F0.imprint","IMPRINT",EDGE,{"disambiguationData":[TD([[subQ2,-1.0]])],"derivedFrom":subQ1}),-1.0]])]});}
            var Q55;
            {var subQ0=sQuery(id+"F0.wireOp",EDGE,"E48.3.0.2");var subQ1=sQuery(id+"F0.wireOp",EDGE,"E38.top");var subQ2=makeQuery(id+"F0.imprint","INTERSECT",VERTEX,{"derivedFrom":[subQ1,subQ0]});Q55=makeQuery(id+"F0.imprint","IMPRINT",FACE,{"disambiguationData":[TD([[makeQuery(id+"F0.imprint","IMPRINT",EDGE,{"disambiguationData":[TD([[subQ2,-1.0]])],"derivedFrom":subQ1}),-1.0]])]});}
            var Q56;
            {var subQ0=sQuery(id+"F0.wireOp",EDGE,"E48.3.0.3");var subQ1=sQuery(id+"F0.wireOp",EDGE,"E38.top");var subQ2=makeQuery(id+"F0.imprint","INTERSECT",VERTEX,{"derivedFrom":[subQ1,subQ0]});Q56=makeQuery(id+"F0.imprint","IMPRINT",FACE,{"disambiguationData":[TD([[makeQuery(id+"F0.imprint","IMPRINT",EDGE,{"disambiguationData":[TD([[subQ2,-1.0]])],"derivedFrom":subQ1}),-1.0]])]});}
            var Q57;
            {var subQ0=sQuery(id+"F0.wireOp",EDGE,"E48.2.0.2");var subQ1=sQuery(id+"F0.wireOp",EDGE,"E38.top");var subQ2=makeQuery(id+"F0.imprint","INTERSECT",VERTEX,{"derivedFrom":[subQ1,subQ0]});Q57=makeQuery(id+"F0.imprint","IMPRINT",FACE,{"disambiguationData":[TD([[makeQuery(id+"F0.imprint","IMPRINT",EDGE,{"disambiguationData":[TD([[subQ2,-1.0]])],"derivedFrom":subQ1}),-1.0]])]});}
            var Q58;
            {var subQ0=sQuery(id+"F0.wireOp",EDGE,"E48.2.0.3");var subQ1=sQuery(id+"F0.wireOp",EDGE,"E38.top");var subQ2=makeQuery(id+"F0.imprint","INTERSECT",VERTEX,{"derivedFrom":[subQ1,subQ0]});Q58=makeQuery(id+"F0.imprint","IMPRINT",FACE,{"disambiguationData":[TD([[makeQuery(id+"F0.imprint","IMPRINT",EDGE,{"disambiguationData":[TD([[subQ2,-1.0]])],"derivedFrom":subQ1}),-1.0]])]});}
            var Q59;
            {var subQ0=sQuery(id+"F0.wireOp",EDGE,"E48.1.0.2");var subQ1=sQuery(id+"F0.wireOp",EDGE,"E38.top");var subQ2=makeQuery(id+"F0.imprint","INTERSECT",VERTEX,{"derivedFrom":[subQ1,subQ0]});Q59=makeQuery(id+"F0.imprint","IMPRINT",FACE,{"disambiguationData":[TD([[makeQuery(id+"F0.imprint","IMPRINT",EDGE,{"disambiguationData":[TD([[subQ2,-1.0]])],"derivedFrom":subQ1}),-1.0]])]});}
            var Q60;
            {var subQ0=sQuery(id+"F0.wireOp",EDGE,"E48.1.0.3");var subQ1=sQuery(id+"F0.wireOp",EDGE,"E38.top");var subQ2=makeQuery(id+"F0.imprint","INTERSECT",VERTEX,{"derivedFrom":[subQ1,subQ0]});Q60=makeQuery(id+"F0.imprint","IMPRINT",FACE,{"disambiguationData":[TD([[makeQuery(id+"F0.imprint","IMPRINT",EDGE,{"disambiguationData":[TD([[subQ2,-1.0]])],"derivedFrom":subQ1}),-1.0]])]});}
            extrude(context, id + "F1", {"entities" : qUnion([Q0, Q1, Q2, Q3, Q4, Q5, Q6, Q7, Q8, Q9, Q10, Q11, Q12, Q13, Q14, Q15, Q16, Q17, Q18, Q19, Q20, Q21, Q22, Q23, Q24, Q25, Q26, Q27, Q28, Q29, Q30, Q31, Q32, Q33, Q34, Q35, Q36, Q37, Q38, Q39, Q40, Q41, Q42, Q43, Q44, Q45, Q46, Q47, Q48, Q49, Q50, Q51, Q52, Q53, Q54, Q55, Q56, Q57, Q58, Q59, Q60]), "depth" : 1 / 101.6 * mm});
        }
        {
            var Q0;
            Q0=makeQuery(id+"F1.opExtrude","SWEPT_FACE",FACE,{"disambiguationData":[OSD([sQuery(id+"F0.wireOp",EDGE,"E0.top")])]});
            var sketch = newSketch(context, id + "F2", { "sketchPlane" : qUnion([Q0])});
            skLineSegment(sketch, "E49.bottom", {"start": v(-98.75, 0) * mm, "end": v(-91.25, 0) * mm});
            skLineSegment(sketch, "E49.top", {"start": v(-98.75, -6.35) * mm, "end": v(-91.25, -6.35) * mm});
            skLineSegment(sketch, "E49.left", {"start": v(-98.75, 0) * mm, "end": v(-98.75, -6.35) * mm});
            skLineSegment(sketch, "E49.right", {"start": v(-91.25, 0) * mm, "end": v(-91.25, -6.35) * mm});
            skLineSegment(sketch, "E50.1.0.0", {"start": v(-68.75, 0) * mm, "end": v(-68.75, -6.35) * mm});
            skLineSegment(sketch, "E50.1.0.1", {"start": v(-76.25, 0) * mm, "end": v(-68.75, 0) * mm});
            skLineSegment(sketch, "E50.1.0.2", {"start": v(-76.25, 0) * mm, "end": v(-76.25, -6.35) * mm});
            skLineSegment(sketch, "E50.1.0.3", {"start": v(-76.25, -6.35) * mm, "end": v(-68.75, -6.35) * mm});
            skLineSegment(sketch, "E50.2.0.0", {"start": v(-46.25, 0) * mm, "end": v(-46.25, -6.35) * mm});
            skLineSegment(sketch, "E50.2.0.1", {"start": v(-53.75, 0) * mm, "end": v(-46.25, 0) * mm});
            skLineSegment(sketch, "E50.2.0.2", {"start": v(-53.75, 0) * mm, "end": v(-53.75, -6.35) * mm});
            skLineSegment(sketch, "E50.2.0.3", {"start": v(-53.75, -6.35) * mm, "end": v(-46.25, -6.35) * mm});
            skLineSegment(sketch, "E50.3.0.0", {"start": v(-23.75, 0) * mm, "end": v(-23.75, -6.35) * mm});
            skLineSegment(sketch, "E50.3.0.1", {"start": v(-31.25, 0) * mm, "end": v(-23.75, 0) * mm});
            skLineSegment(sketch, "E50.3.0.2", {"start": v(-31.25, 0) * mm, "end": v(-31.25, -6.35) * mm});
            skLineSegment(sketch, "E50.3.0.3", {"start": v(-31.25, -6.35) * mm, "end": v(-23.75, -6.35) * mm});
            skLineSegment(sketch, "E50.4.0.0", {"start": v(-1.25, 0) * mm, "end": v(-1.25, -6.35) * mm});
            skLineSegment(sketch, "E50.4.0.1", {"start": v(-8.75, 0) * mm, "end": v(-1.25, 0) * mm});
            skLineSegment(sketch, "E50.4.0.2", {"start": v(-8.75, 0) * mm, "end": v(-8.75, -6.35) * mm});
            skLineSegment(sketch, "E50.4.0.3", {"start": v(-8.75, -6.35) * mm, "end": v(-1.25, -6.35) * mm});
            skLineSegment(sketch, "E50.5.0.0", {"start": v(21.25, 0) * mm, "end": v(21.25, -6.35) * mm});
            skLineSegment(sketch, "E50.5.0.1", {"start": v(13.75, 0) * mm, "end": v(21.25, 0) * mm});
            skLineSegment(sketch, "E50.5.0.2", {"start": v(13.75, 0) * mm, "end": v(13.75, -6.35) * mm});
            skLineSegment(sketch, "E50.5.0.3", {"start": v(13.75, -6.35) * mm, "end": v(21.25, -6.35) * mm});
            skLineSegment(sketch, "E50.6.0.0", {"start": v(43.75, 0) * mm, "end": v(43.75, -6.35) * mm});
            skLineSegment(sketch, "E50.6.0.1", {"start": v(36.25, 0) * mm, "end": v(43.75, 0) * mm});
            skLineSegment(sketch, "E50.6.0.2", {"start": v(36.25, 0) * mm, "end": v(36.25, -6.35) * mm});
            skLineSegment(sketch, "E50.6.0.3", {"start": v(36.25, -6.35) * mm, "end": v(43.75, -6.35) * mm});
            skLineSegment(sketch, "E50.direction1", {"start": v(-91.25, -6.35) * mm, "end": v(-68.75, -6.35) * mm, "construction": true});
            skSolve(sketch);
        }
        {
            var Q0;
            Q0=makeQuery(id+"F2.imprint","IMPRINT",FACE,{"disambiguationData":[TD([[makeQuery(id+"F2.imprint","IMPRINT",EDGE,{"derivedFrom":sQuery(id+"F2.wireOp",EDGE,"E49.bottom")}),1.0]])]});
            var Q1;
            Q1=makeQuery(id+"F2.imprint","IMPRINT",FACE,{"disambiguationData":[TD([[makeQuery(id+"F2.imprint","IMPRINT",EDGE,{"derivedFrom":sQuery(id+"F2.wireOp",EDGE,"E50.1.0.0")}),-1.0]])]});
            var Q2;
            Q2=makeQuery(id+"F2.imprint","IMPRINT",FACE,{"disambiguationData":[TD([[makeQuery(id+"F2.imprint","IMPRINT",EDGE,{"derivedFrom":sQuery(id+"F2.wireOp",EDGE,"E50.2.0.0")}),-1.0]])]});
            var Q3;
            Q3=makeQuery(id+"F2.imprint","IMPRINT",FACE,{"disambiguationData":[TD([[makeQuery(id+"F2.imprint","IMPRINT",EDGE,{"derivedFrom":sQuery(id+"F2.wireOp",EDGE,"E50.3.0.0")}),-1.0]])]});
            var Q4;
            Q4=makeQuery(id+"F2.imprint","IMPRINT",FACE,{"disambiguationData":[TD([[makeQuery(id+"F2.imprint","IMPRINT",EDGE,{"derivedFrom":sQuery(id+"F2.wireOp",EDGE,"E50.4.0.0")}),-1.0]])]});
            var Q5;
            Q5=makeQuery(id+"F2.imprint","IMPRINT",FACE,{"disambiguationData":[TD([[makeQuery(id+"F2.imprint","IMPRINT",EDGE,{"derivedFrom":sQuery(id+"F2.wireOp",EDGE,"E50.5.0.0")}),-1.0]])]});
            var Q6;
            Q6=makeQuery(id+"F2.imprint","IMPRINT",FACE,{"disambiguationData":[TD([[makeQuery(id+"F2.imprint","IMPRINT",EDGE,{"derivedFrom":sQuery(id+"F2.wireOp",EDGE,"E50.6.0.0")}),-1.0]])]});
            extrude(context, id + "F3", {"entities" : qUnion([Q0, Q1, Q2, Q3, Q4, Q5, Q6]), "operationType" : NewBodyOperationType.ADD, "depth" : 1 / 101.6 * mm});
        }
        {
            var Q0;
            Q0=makeQuery(id+"F1.opExtrude","SWEPT_FACE",FACE,{"disambiguationData":[OSD([sQuery(id+"F0.wireOp",EDGE,"E38.top")])]});
            extrude(context, id + "F4", {"entities" : qUnion([Q0]), "operationType" : NewBodyOperationType.REMOVE, "oppositeDirection" : true, "depth" : 2.5 * mm});
        }
        {
            var Q0;
            Q0=makeQuery(id+"F3.boolean.opBoolean","MERGE",FACE,{"derivedFrom":[makeQuery(id+"F1.opExtrude","SWEPT_FACE",FACE,{"disambiguationData":[OSD([sQuery(id+"F0.wireOp",EDGE,"E0.right")])]}),makeQuery(id+"F3.opExtrude","SWEPT_FACE",FACE,{"disambiguationData":[OSD([sQuery(id+"F2.wireOp",EDGE,"E49.left")])]})]});
            var sketch = newSketch(context, id + "F5", { "sketchPlane" : qUnion([Q0])});
            skLineSegment(sketch, "E51.bottom", {"start": v(0, -5) * mm, "end": v(6.35, -5) * mm});
            skLineSegment(sketch, "E51.top", {"start": v(0, 1.35) * mm, "end": v(6.35, 1.35) * mm});
            skLineSegment(sketch, "E51.left", {"start": v(0, -5) * mm, "end": v(0, 1.35) * mm});
            skLineSegment(sketch, "E51.right", {"start": v(6.35, -5) * mm, "end": v(6.35, 1.35) * mm});
            skSolve(sketch);
        }
        {
            var Q0;
            {var subQ0=sQuery(id+"F0.wireOp",EDGE,"E44");var subQ1=sQuery(id+"F0.wireOp",EDGE,"E38.bottom");var subQ2=makeQuery(id+"F0.imprint","INTERSECT",VERTEX,{"derivedFrom":[subQ1,subQ0]});Q0=makeQuery(id+"F0.imprint","IMPRINT",FACE,{"disambiguationData":[TD([[makeQuery(id+"F0.imprint","IMPRINT",EDGE,{"disambiguationData":[TD([[subQ2,-1.0]])],"derivedFrom":subQ1}),-1.0]])]});}
            var Q1;
            {var subQ0=sQuery(id+"F0.wireOp",EDGE,"E44");var subQ1=sQuery(id+"F0.wireOp",EDGE,"E38.top");var subQ2=makeQuery(id+"F0.imprint","INTERSECT",VERTEX,{"derivedFrom":[subQ1,subQ0]});Q1=makeQuery(id+"F0.imprint","IMPRINT",FACE,{"disambiguationData":[TD([[makeQuery(id+"F0.imprint","IMPRINT",EDGE,{"disambiguationData":[TD([[subQ2,-1.0]])],"derivedFrom":subQ1}),1.0]])]});}
            var Q2;
            {var subQ1=sQuery(id+"F0.wireOp",EDGE,"E38.top");var subQ7=sQuery(id+"F0.wireOp",EDGE,"E43");var subQ9=makeQuery(id+"F0.imprint","INTERSECT",VERTEX,{"derivedFrom":[subQ1,subQ7]});Q2=makeQuery(id+"F0.imprint","IMPRINT",FACE,{"disambiguationData":[TD([[makeQuery(id+"F0.imprint","IMPRINT",EDGE,{"disambiguationData":[TD([[subQ9,-1.0]])],"derivedFrom":subQ1}),1.0]])]});}
            var Q3;
            {var subQ0=sQuery(id+"F0.wireOp",EDGE,"E46");var subQ1=sQuery(id+"F0.wireOp",EDGE,"E38.top");var subQ2=makeQuery(id+"F0.imprint","INTERSECT",VERTEX,{"derivedFrom":[subQ1,subQ0]});Q3=makeQuery(id+"F0.imprint","IMPRINT",FACE,{"disambiguationData":[TD([[makeQuery(id+"F0.imprint","IMPRINT",EDGE,{"disambiguationData":[TD([[subQ2,-1.0]])],"derivedFrom":subQ1}),-1.0]])]});}
            var Q4;
            {var subQ0=sQuery(id+"F0.wireOp",EDGE,"E43");var subQ1=sQuery(id+"F0.wireOp",EDGE,"E38.top");var subQ2=makeQuery(id+"F0.imprint","INTERSECT",VERTEX,{"derivedFrom":[subQ1,subQ0]});Q4=makeQuery(id+"F0.imprint","IMPRINT",FACE,{"disambiguationData":[TD([[makeQuery(id+"F0.imprint","IMPRINT",EDGE,{"disambiguationData":[TD([[subQ2,-1.0]])],"derivedFrom":subQ1}),-1.0]])]});}
            var Q5;
            {var subQ0=sQuery(id+"F0.wireOp",EDGE,"E43");var subQ3=sQuery(id+"F0.wireOp",EDGE,"E45");var subQ5=makeQuery(id+"F0.imprint","INTERSECT",VERTEX,{"derivedFrom":[subQ0,subQ3]});Q5=makeQuery(id+"F0.imprint","IMPRINT",FACE,{"disambiguationData":[TD([[makeQuery(id+"F0.imprint","IMPRINT",EDGE,{"disambiguationData":[TD([[subQ5,1.0]])],"derivedFrom":subQ0}),1.0]])]});}
            var Q6;
            {var subQ0=sQuery(id+"F0.wireOp",EDGE,"E42");var subQ1=sQuery(id+"F0.wireOp",EDGE,"E38.top");var subQ2=makeQuery(id+"F0.imprint","INTERSECT",VERTEX,{"derivedFrom":[subQ1,subQ0]});Q6=makeQuery(id+"F0.imprint","IMPRINT",FACE,{"disambiguationData":[TD([[makeQuery(id+"F0.imprint","IMPRINT",EDGE,{"disambiguationData":[TD([[subQ2,-1.0]])],"derivedFrom":subQ1}),1.0]])]});}
            var Q7;
            {var subQ1=sQuery(id+"F0.wireOp",EDGE,"E38.top");var subQ5=sQuery(id+"F0.wireOp",EDGE,"E46");var subQ6=makeQuery(id+"F0.imprint","INTERSECT",VERTEX,{"derivedFrom":[subQ1,subQ5]});Q7=makeQuery(id+"F0.imprint","IMPRINT",FACE,{"disambiguationData":[TD([[makeQuery(id+"F0.imprint","IMPRINT",EDGE,{"disambiguationData":[TD([[subQ6,-1.0]])],"derivedFrom":subQ1}),1.0]])]});}
            var Q8;
            {var subQ1=sQuery(id+"F0.wireOp",EDGE,"E38.top");var subQ7=sQuery(id+"F0.wireOp",EDGE,"E48.1.0.3");var subQ9=makeQuery(id+"F0.imprint","INTERSECT",VERTEX,{"derivedFrom":[subQ1,subQ7]});Q8=makeQuery(id+"F0.imprint","IMPRINT",FACE,{"disambiguationData":[TD([[makeQuery(id+"F0.imprint","IMPRINT",EDGE,{"disambiguationData":[TD([[subQ9,-1.0]])],"derivedFrom":subQ1}),1.0]])]});}
            var Q9;
            {var subQ0=sQuery(id+"F0.wireOp",EDGE,"E48.1.0.3");var subQ1=sQuery(id+"F0.wireOp",EDGE,"E38.top");var subQ2=makeQuery(id+"F0.imprint","INTERSECT",VERTEX,{"derivedFrom":[subQ1,subQ0]});Q9=makeQuery(id+"F0.imprint","IMPRINT",FACE,{"disambiguationData":[TD([[makeQuery(id+"F0.imprint","IMPRINT",EDGE,{"disambiguationData":[TD([[subQ2,-1.0]])],"derivedFrom":subQ1}),-1.0]])]});}
            var Q10;
            {var subQ0=sQuery(id+"F0.wireOp",EDGE,"E48.1.0.2");var subQ1=sQuery(id+"F0.wireOp",EDGE,"E38.top");var subQ2=makeQuery(id+"F0.imprint","INTERSECT",VERTEX,{"derivedFrom":[subQ1,subQ0]});Q10=makeQuery(id+"F0.imprint","IMPRINT",FACE,{"disambiguationData":[TD([[makeQuery(id+"F0.imprint","IMPRINT",EDGE,{"disambiguationData":[TD([[subQ2,-1.0]])],"derivedFrom":subQ1}),-1.0]])]});}
            var Q11;
            {var subQ3=sQuery(id+"F0.wireOp",EDGE,"E48.1.0.2");var subQ6=sQuery(id+"F0.wireOp",EDGE,"E38.top");var subQ9=makeQuery(id+"F0.imprint","INTERSECT",VERTEX,{"derivedFrom":[subQ6,subQ3]});Q11=makeQuery(id+"F0.imprint","IMPRINT",FACE,{"disambiguationData":[TD([[makeQuery(id+"F0.imprint","IMPRINT",EDGE,{"disambiguationData":[TD([[subQ9,-1.0]])],"derivedFrom":subQ6}),1.0]])]});}
            var Q12;
            {var subQ0=sQuery(id+"F0.wireOp",EDGE,"E48.1.0.0");var subQ3=sQuery(id+"F0.wireOp",EDGE,"E48.2.0.3");var subQ5=makeQuery(id+"F0.imprint","INTERSECT",VERTEX,{"derivedFrom":[subQ0,subQ3]});Q12=makeQuery(id+"F0.imprint","IMPRINT",FACE,{"disambiguationData":[TD([[makeQuery(id+"F0.imprint","IMPRINT",EDGE,{"disambiguationData":[TD([[subQ5,-1.0]])],"derivedFrom":subQ0}),1.0]])]});}
            var Q13;
            {var subQ5=sQuery(id+"F0.wireOp",EDGE,"E38.top");var subQ7=sQuery(id+"F0.wireOp",EDGE,"E48.2.0.3");var subQ8=makeQuery(id+"F0.imprint","INTERSECT",VERTEX,{"derivedFrom":[subQ5,subQ7]});Q13=makeQuery(id+"F0.imprint","IMPRINT",FACE,{"disambiguationData":[TD([[makeQuery(id+"F0.imprint","IMPRINT",EDGE,{"disambiguationData":[TD([[subQ8,-1.0]])],"derivedFrom":subQ5}),1.0]])]});}
            var Q14;
            {var subQ0=sQuery(id+"F0.wireOp",EDGE,"E48.2.0.3");var subQ1=sQuery(id+"F0.wireOp",EDGE,"E38.top");var subQ2=makeQuery(id+"F0.imprint","INTERSECT",VERTEX,{"derivedFrom":[subQ1,subQ0]});Q14=makeQuery(id+"F0.imprint","IMPRINT",FACE,{"disambiguationData":[TD([[makeQuery(id+"F0.imprint","IMPRINT",EDGE,{"disambiguationData":[TD([[subQ2,-1.0]])],"derivedFrom":subQ1}),-1.0]])]});}
            var Q15;
            {var subQ0=sQuery(id+"F0.wireOp",EDGE,"E48.2.0.1");var subQ1=sQuery(id+"F0.wireOp",EDGE,"E38.top");var subQ2=makeQuery(id+"F0.imprint","INTERSECT",VERTEX,{"derivedFrom":[subQ1,subQ0]});Q15=makeQuery(id+"F0.imprint","IMPRINT",FACE,{"disambiguationData":[TD([[makeQuery(id+"F0.imprint","IMPRINT",EDGE,{"disambiguationData":[TD([[subQ2,-1.0]])],"derivedFrom":subQ1}),1.0]])]});}
            var Q16;
            {var subQ0=sQuery(id+"F0.wireOp",EDGE,"E48.2.0.2");var subQ1=sQuery(id+"F0.wireOp",EDGE,"E38.top");var subQ2=makeQuery(id+"F0.imprint","INTERSECT",VERTEX,{"derivedFrom":[subQ1,subQ0]});Q16=makeQuery(id+"F0.imprint","IMPRINT",FACE,{"disambiguationData":[TD([[makeQuery(id+"F0.imprint","IMPRINT",EDGE,{"disambiguationData":[TD([[subQ2,-1.0]])],"derivedFrom":subQ1}),-1.0]])]});}
            var Q17;
            {var subQ1=sQuery(id+"F0.wireOp",EDGE,"E38.top");var subQ5=sQuery(id+"F0.wireOp",EDGE,"E48.2.0.2");var subQ6=makeQuery(id+"F0.imprint","INTERSECT",VERTEX,{"derivedFrom":[subQ1,subQ5]});Q17=makeQuery(id+"F0.imprint","IMPRINT",FACE,{"disambiguationData":[TD([[makeQuery(id+"F0.imprint","IMPRINT",EDGE,{"disambiguationData":[TD([[subQ6,-1.0]])],"derivedFrom":subQ1}),1.0]])]});}
            var Q18;
            {var subQ0=sQuery(id+"F0.wireOp",EDGE,"E48.2.0.0");var subQ3=sQuery(id+"F0.wireOp",EDGE,"E48.3.0.3");var subQ5=makeQuery(id+"F0.imprint","INTERSECT",VERTEX,{"derivedFrom":[subQ0,subQ3]});Q18=makeQuery(id+"F0.imprint","IMPRINT",FACE,{"disambiguationData":[TD([[makeQuery(id+"F0.imprint","IMPRINT",EDGE,{"disambiguationData":[TD([[subQ5,-1.0]])],"derivedFrom":subQ0}),1.0]])]});}
            var Q19;
            {var subQ1=sQuery(id+"F0.wireOp",EDGE,"E38.top");var subQ7=sQuery(id+"F0.wireOp",EDGE,"E48.3.0.3");var subQ9=makeQuery(id+"F0.imprint","INTERSECT",VERTEX,{"derivedFrom":[subQ1,subQ7]});Q19=makeQuery(id+"F0.imprint","IMPRINT",FACE,{"disambiguationData":[TD([[makeQuery(id+"F0.imprint","IMPRINT",EDGE,{"disambiguationData":[TD([[subQ9,-1.0]])],"derivedFrom":subQ1}),1.0]])]});}
            var Q20;
            {var subQ0=sQuery(id+"F0.wireOp",EDGE,"E48.3.0.3");var subQ1=sQuery(id+"F0.wireOp",EDGE,"E38.top");var subQ2=makeQuery(id+"F0.imprint","INTERSECT",VERTEX,{"derivedFrom":[subQ1,subQ0]});Q20=makeQuery(id+"F0.imprint","IMPRINT",FACE,{"disambiguationData":[TD([[makeQuery(id+"F0.imprint","IMPRINT",EDGE,{"disambiguationData":[TD([[subQ2,-1.0]])],"derivedFrom":subQ1}),-1.0]])]});}
            var Q21;
            {var subQ0=sQuery(id+"F0.wireOp",EDGE,"E48.1.0.1");var subQ1=sQuery(id+"F0.wireOp",EDGE,"E38.top");var subQ2=makeQuery(id+"F0.imprint","INTERSECT",VERTEX,{"derivedFrom":[subQ1,subQ0]});Q21=makeQuery(id+"F0.imprint","IMPRINT",FACE,{"disambiguationData":[TD([[makeQuery(id+"F0.imprint","IMPRINT",EDGE,{"disambiguationData":[TD([[subQ2,-1.0]])],"derivedFrom":subQ1}),1.0]])]});}
            var Q22;
            {var subQ0=sQuery(id+"F0.wireOp",EDGE,"E48.3.0.2");var subQ1=sQuery(id+"F0.wireOp",EDGE,"E38.top");var subQ2=makeQuery(id+"F0.imprint","INTERSECT",VERTEX,{"derivedFrom":[subQ1,subQ0]});Q22=makeQuery(id+"F0.imprint","IMPRINT",FACE,{"disambiguationData":[TD([[makeQuery(id+"F0.imprint","IMPRINT",EDGE,{"disambiguationData":[TD([[subQ2,-1.0]])],"derivedFrom":subQ1}),-1.0]])]});}
            var Q23;
            {var subQ0=sQuery(id+"F0.wireOp",EDGE,"E48.3.0.2");var subQ1=sQuery(id+"F0.wireOp",EDGE,"E38.top");var subQ2=makeQuery(id+"F0.imprint","INTERSECT",VERTEX,{"derivedFrom":[subQ1,subQ0]});Q23=makeQuery(id+"F0.imprint","IMPRINT",FACE,{"disambiguationData":[TD([[makeQuery(id+"F0.imprint","IMPRINT",EDGE,{"disambiguationData":[TD([[subQ2,-1.0]])],"derivedFrom":subQ1}),1.0]])]});}
            var Q24;
            {var subQ0=sQuery(id+"F0.wireOp",EDGE,"E48.3.0.0");var subQ3=sQuery(id+"F0.wireOp",EDGE,"E48.4.0.3");var subQ5=makeQuery(id+"F0.imprint","INTERSECT",VERTEX,{"derivedFrom":[subQ0,subQ3]});Q24=makeQuery(id+"F0.imprint","IMPRINT",FACE,{"disambiguationData":[TD([[makeQuery(id+"F0.imprint","IMPRINT",EDGE,{"disambiguationData":[TD([[subQ5,-1.0]])],"derivedFrom":subQ0}),1.0]])]});}
            var Q25;
            {var subQ1=sQuery(id+"F0.wireOp",EDGE,"E38.top");var subQ7=sQuery(id+"F0.wireOp",EDGE,"E48.4.0.3");var subQ9=makeQuery(id+"F0.imprint","INTERSECT",VERTEX,{"derivedFrom":[subQ1,subQ7]});Q25=makeQuery(id+"F0.imprint","IMPRINT",FACE,{"disambiguationData":[TD([[makeQuery(id+"F0.imprint","IMPRINT",EDGE,{"disambiguationData":[TD([[subQ9,-1.0]])],"derivedFrom":subQ1}),1.0]])]});}
            var Q26;
            {var subQ0=sQuery(id+"F0.wireOp",EDGE,"E48.4.0.3");var subQ1=sQuery(id+"F0.wireOp",EDGE,"E38.top");var subQ2=makeQuery(id+"F0.imprint","INTERSECT",VERTEX,{"derivedFrom":[subQ1,subQ0]});Q26=makeQuery(id+"F0.imprint","IMPRINT",FACE,{"disambiguationData":[TD([[makeQuery(id+"F0.imprint","IMPRINT",EDGE,{"disambiguationData":[TD([[subQ2,-1.0]])],"derivedFrom":subQ1}),-1.0]])]});}
            var Q27;
            {var subQ0=sQuery(id+"F0.wireOp",EDGE,"E48.4.0.2");var subQ1=sQuery(id+"F0.wireOp",EDGE,"E38.top");var subQ2=makeQuery(id+"F0.imprint","INTERSECT",VERTEX,{"derivedFrom":[subQ1,subQ0]});Q27=makeQuery(id+"F0.imprint","IMPRINT",FACE,{"disambiguationData":[TD([[makeQuery(id+"F0.imprint","IMPRINT",EDGE,{"disambiguationData":[TD([[subQ2,-1.0]])],"derivedFrom":subQ1}),-1.0]])]});}
            var Q28;
            {var subQ0=sQuery(id+"F0.wireOp",EDGE,"E48.4.0.1");var subQ1=sQuery(id+"F0.wireOp",EDGE,"E38.top");var subQ2=makeQuery(id+"F0.imprint","INTERSECT",VERTEX,{"derivedFrom":[subQ1,subQ0]});Q28=makeQuery(id+"F0.imprint","IMPRINT",FACE,{"disambiguationData":[TD([[makeQuery(id+"F0.imprint","IMPRINT",EDGE,{"disambiguationData":[TD([[subQ2,-1.0]])],"derivedFrom":subQ1}),1.0]])]});}
            var Q29;
            {var subQ3=sQuery(id+"F0.wireOp",EDGE,"E48.4.0.2");var subQ6=sQuery(id+"F0.wireOp",EDGE,"E38.top");var subQ9=makeQuery(id+"F0.imprint","INTERSECT",VERTEX,{"derivedFrom":[subQ6,subQ3]});Q29=makeQuery(id+"F0.imprint","IMPRINT",FACE,{"disambiguationData":[TD([[makeQuery(id+"F0.imprint","IMPRINT",EDGE,{"disambiguationData":[TD([[subQ9,-1.0]])],"derivedFrom":subQ6}),1.0]])]});}
            var Q30;
            {var subQ0=sQuery(id+"F0.wireOp",EDGE,"E48.4.0.0");var subQ3=sQuery(id+"F0.wireOp",EDGE,"E48.5.0.3");var subQ5=makeQuery(id+"F0.imprint","INTERSECT",VERTEX,{"derivedFrom":[subQ0,subQ3]});Q30=makeQuery(id+"F0.imprint","IMPRINT",FACE,{"disambiguationData":[TD([[makeQuery(id+"F0.imprint","IMPRINT",EDGE,{"disambiguationData":[TD([[subQ5,-1.0]])],"derivedFrom":subQ0}),1.0]])]});}
            var Q31;
            {var subQ1=sQuery(id+"F0.wireOp",EDGE,"E38.top");var subQ7=sQuery(id+"F0.wireOp",EDGE,"E48.5.0.3");var subQ9=makeQuery(id+"F0.imprint","INTERSECT",VERTEX,{"derivedFrom":[subQ1,subQ7]});Q31=makeQuery(id+"F0.imprint","IMPRINT",FACE,{"disambiguationData":[TD([[makeQuery(id+"F0.imprint","IMPRINT",EDGE,{"disambiguationData":[TD([[subQ9,-1.0]])],"derivedFrom":subQ1}),1.0]])]});}
            var Q32;
            {var subQ0=sQuery(id+"F0.wireOp",EDGE,"E48.5.0.3");var subQ1=sQuery(id+"F0.wireOp",EDGE,"E38.top");var subQ2=makeQuery(id+"F0.imprint","INTERSECT",VERTEX,{"derivedFrom":[subQ1,subQ0]});Q32=makeQuery(id+"F0.imprint","IMPRINT",FACE,{"disambiguationData":[TD([[makeQuery(id+"F0.imprint","IMPRINT",EDGE,{"disambiguationData":[TD([[subQ2,-1.0]])],"derivedFrom":subQ1}),-1.0]])]});}
            var Q33;
            {var subQ0=sQuery(id+"F0.wireOp",EDGE,"E48.5.0.1");var subQ1=sQuery(id+"F0.wireOp",EDGE,"E38.top");var subQ2=makeQuery(id+"F0.imprint","INTERSECT",VERTEX,{"derivedFrom":[subQ1,subQ0]});Q33=makeQuery(id+"F0.imprint","IMPRINT",FACE,{"disambiguationData":[TD([[makeQuery(id+"F0.imprint","IMPRINT",EDGE,{"disambiguationData":[TD([[subQ2,-1.0]])],"derivedFrom":subQ1}),1.0]])]});}
            var Q34;
            {var subQ0=sQuery(id+"F0.wireOp",EDGE,"E48.5.0.2");var subQ1=sQuery(id+"F0.wireOp",EDGE,"E38.top");var subQ2=makeQuery(id+"F0.imprint","INTERSECT",VERTEX,{"derivedFrom":[subQ1,subQ0]});Q34=makeQuery(id+"F0.imprint","IMPRINT",FACE,{"disambiguationData":[TD([[makeQuery(id+"F0.imprint","IMPRINT",EDGE,{"disambiguationData":[TD([[subQ2,-1.0]])],"derivedFrom":subQ1}),-1.0]])]});}
            var Q35;
            {var subQ0=sQuery(id+"F0.wireOp",EDGE,"E48.5.0.2");var subQ1=sQuery(id+"F0.wireOp",EDGE,"E38.top");var subQ2=makeQuery(id+"F0.imprint","INTERSECT",VERTEX,{"derivedFrom":[subQ1,subQ0]});Q35=makeQuery(id+"F0.imprint","IMPRINT",FACE,{"disambiguationData":[TD([[makeQuery(id+"F0.imprint","IMPRINT",EDGE,{"disambiguationData":[TD([[subQ2,-1.0]])],"derivedFrom":subQ1}),1.0]])]});}
            var Q36;
            {var subQ0=sQuery(id+"F0.wireOp",EDGE,"E48.5.0.0");var subQ3=sQuery(id+"F0.wireOp",EDGE,"E48.6.0.3");var subQ5=makeQuery(id+"F0.imprint","INTERSECT",VERTEX,{"derivedFrom":[subQ0,subQ3]});Q36=makeQuery(id+"F0.imprint","IMPRINT",FACE,{"disambiguationData":[TD([[makeQuery(id+"F0.imprint","IMPRINT",EDGE,{"disambiguationData":[TD([[subQ5,-1.0]])],"derivedFrom":subQ0}),1.0]])]});}
            var Q37;
            {var subQ5=sQuery(id+"F0.wireOp",EDGE,"E48.6.0.3");var subQ6=sQuery(id+"F0.wireOp",EDGE,"E38.top");var subQ7=makeQuery(id+"F0.imprint","INTERSECT",VERTEX,{"derivedFrom":[subQ6,subQ5]});Q37=makeQuery(id+"F0.imprint","IMPRINT",FACE,{"disambiguationData":[TD([[makeQuery(id+"F0.imprint","IMPRINT",EDGE,{"disambiguationData":[TD([[subQ7,-1.0]])],"derivedFrom":subQ6}),1.0]])]});}
            var Q38;
            {var subQ0=sQuery(id+"F0.wireOp",EDGE,"E48.6.0.2");var subQ1=sQuery(id+"F0.wireOp",EDGE,"E38.top");var subQ2=makeQuery(id+"F0.imprint","INTERSECT",VERTEX,{"derivedFrom":[subQ1,subQ0]});Q38=makeQuery(id+"F0.imprint","IMPRINT",FACE,{"disambiguationData":[TD([[makeQuery(id+"F0.imprint","IMPRINT",EDGE,{"disambiguationData":[TD([[subQ2,-1.0]])],"derivedFrom":subQ1}),-1.0]])]});}
            var Q39;
            {var subQ0=sQuery(id+"F0.wireOp",EDGE,"E48.6.0.3");var subQ1=sQuery(id+"F0.wireOp",EDGE,"E38.top");var subQ2=makeQuery(id+"F0.imprint","INTERSECT",VERTEX,{"derivedFrom":[subQ1,subQ0]});Q39=makeQuery(id+"F0.imprint","IMPRINT",FACE,{"disambiguationData":[TD([[makeQuery(id+"F0.imprint","IMPRINT",EDGE,{"disambiguationData":[TD([[subQ2,-1.0]])],"derivedFrom":subQ1}),-1.0]])]});}
            var Q40;
            {var subQ0=sQuery(id+"F0.wireOp",EDGE,"E48.6.0.2");var subQ1=sQuery(id+"F0.wireOp",EDGE,"E38.top");var subQ2=makeQuery(id+"F0.imprint","INTERSECT",VERTEX,{"derivedFrom":[subQ1,subQ0]});Q40=makeQuery(id+"F0.imprint","IMPRINT",FACE,{"disambiguationData":[TD([[makeQuery(id+"F0.imprint","IMPRINT",EDGE,{"disambiguationData":[TD([[subQ2,-1.0]])],"derivedFrom":subQ1}),1.0]])]});}
            var Q41;
            {var subQ0=sQuery(id+"F0.wireOp",EDGE,"E48.6.0.1");var subQ1=sQuery(id+"F0.wireOp",EDGE,"E38.top");var subQ2=makeQuery(id+"F0.imprint","INTERSECT",VERTEX,{"derivedFrom":[subQ1,subQ0]});Q41=makeQuery(id+"F0.imprint","IMPRINT",FACE,{"disambiguationData":[TD([[makeQuery(id+"F0.imprint","IMPRINT",EDGE,{"disambiguationData":[TD([[subQ2,-1.0]])],"derivedFrom":subQ1}),1.0]])]});}
            var Q42;
            {var subQ0=sQuery(id+"F0.wireOp",EDGE,"E48.6.0.0");var subQ3=sQuery(id+"F0.wireOp",EDGE,"E48.7.0.3");var subQ5=makeQuery(id+"F0.imprint","INTERSECT",VERTEX,{"derivedFrom":[subQ0,subQ3]});Q42=makeQuery(id+"F0.imprint","IMPRINT",FACE,{"disambiguationData":[TD([[makeQuery(id+"F0.imprint","IMPRINT",EDGE,{"disambiguationData":[TD([[subQ5,-1.0]])],"derivedFrom":subQ0}),1.0]])]});}
            var Q43;
            {var subQ0=sQuery(id+"F0.wireOp",EDGE,"E48.3.0.1");var subQ1=sQuery(id+"F0.wireOp",EDGE,"E38.top");var subQ2=makeQuery(id+"F0.imprint","INTERSECT",VERTEX,{"derivedFrom":[subQ1,subQ0]});Q43=makeQuery(id+"F0.imprint","IMPRINT",FACE,{"disambiguationData":[TD([[makeQuery(id+"F0.imprint","IMPRINT",EDGE,{"disambiguationData":[TD([[subQ2,-1.0]])],"derivedFrom":subQ1}),1.0]])]});}
            var Q44;
            {var subQ1=sQuery(id+"F0.wireOp",EDGE,"E38.top");var subQ7=sQuery(id+"F0.wireOp",EDGE,"E48.7.0.3");var subQ9=makeQuery(id+"F0.imprint","INTERSECT",VERTEX,{"derivedFrom":[subQ1,subQ7]});Q44=makeQuery(id+"F0.imprint","IMPRINT",FACE,{"disambiguationData":[TD([[makeQuery(id+"F0.imprint","IMPRINT",EDGE,{"disambiguationData":[TD([[subQ9,-1.0]])],"derivedFrom":subQ1}),1.0]])]});}
            var Q45;
            {var subQ0=sQuery(id+"F0.wireOp",EDGE,"E48.7.0.1");var subQ1=sQuery(id+"F0.wireOp",EDGE,"E38.top");var subQ2=makeQuery(id+"F0.imprint","INTERSECT",VERTEX,{"derivedFrom":[subQ1,subQ0]});Q45=makeQuery(id+"F0.imprint","IMPRINT",FACE,{"disambiguationData":[TD([[makeQuery(id+"F0.imprint","IMPRINT",EDGE,{"disambiguationData":[TD([[subQ2,-1.0]])],"derivedFrom":subQ1}),1.0]])]});}
            var Q46;
            {var subQ0=sQuery(id+"F0.wireOp",EDGE,"E48.7.0.3");var subQ1=sQuery(id+"F0.wireOp",EDGE,"E38.top");var subQ2=makeQuery(id+"F0.imprint","INTERSECT",VERTEX,{"derivedFrom":[subQ1,subQ0]});Q46=makeQuery(id+"F0.imprint","IMPRINT",FACE,{"disambiguationData":[TD([[makeQuery(id+"F0.imprint","IMPRINT",EDGE,{"disambiguationData":[TD([[subQ2,-1.0]])],"derivedFrom":subQ1}),-1.0]])]});}
            var Q47;
            {var subQ0=sQuery(id+"F0.wireOp",EDGE,"E48.7.0.2");var subQ1=sQuery(id+"F0.wireOp",EDGE,"E38.top");var subQ2=makeQuery(id+"F0.imprint","INTERSECT",VERTEX,{"derivedFrom":[subQ1,subQ0]});Q47=makeQuery(id+"F0.imprint","IMPRINT",FACE,{"disambiguationData":[TD([[makeQuery(id+"F0.imprint","IMPRINT",EDGE,{"disambiguationData":[TD([[subQ2,-1.0]])],"derivedFrom":subQ1}),-1.0]])]});}
            var Q48;
            {var subQ0=sQuery(id+"F0.wireOp",EDGE,"E48.7.0.2");var subQ1=sQuery(id+"F0.wireOp",EDGE,"E38.top");var subQ2=makeQuery(id+"F0.imprint","INTERSECT",VERTEX,{"derivedFrom":[subQ1,subQ0]});Q48=makeQuery(id+"F0.imprint","IMPRINT",FACE,{"disambiguationData":[TD([[makeQuery(id+"F0.imprint","IMPRINT",EDGE,{"disambiguationData":[TD([[subQ2,-1.0]])],"derivedFrom":subQ1}),1.0]])]});}
            var Q49;
            {var subQ0=sQuery(id+"F0.wireOp",EDGE,"E48.7.0.0");var subQ3=sQuery(id+"F0.wireOp",EDGE,"E48.8.0.3");var subQ5=makeQuery(id+"F0.imprint","INTERSECT",VERTEX,{"derivedFrom":[subQ0,subQ3]});Q49=makeQuery(id+"F0.imprint","IMPRINT",FACE,{"disambiguationData":[TD([[makeQuery(id+"F0.imprint","IMPRINT",EDGE,{"disambiguationData":[TD([[subQ5,-1.0]])],"derivedFrom":subQ0}),1.0]])]});}
            var Q50;
            {var subQ5=sQuery(id+"F0.wireOp",EDGE,"E38.top");var subQ7=sQuery(id+"F0.wireOp",EDGE,"E48.8.0.3");var subQ9=makeQuery(id+"F0.imprint","INTERSECT",VERTEX,{"derivedFrom":[subQ5,subQ7]});Q50=makeQuery(id+"F0.imprint","IMPRINT",FACE,{"disambiguationData":[TD([[makeQuery(id+"F0.imprint","IMPRINT",EDGE,{"disambiguationData":[TD([[subQ9,-1.0]])],"derivedFrom":subQ5}),1.0]])]});}
            var Q51;
            {var subQ0=sQuery(id+"F0.wireOp",EDGE,"E48.8.0.3");var subQ1=sQuery(id+"F0.wireOp",EDGE,"E38.top");var subQ2=makeQuery(id+"F0.imprint","INTERSECT",VERTEX,{"derivedFrom":[subQ1,subQ0]});Q51=makeQuery(id+"F0.imprint","IMPRINT",FACE,{"disambiguationData":[TD([[makeQuery(id+"F0.imprint","IMPRINT",EDGE,{"disambiguationData":[TD([[subQ2,-1.0]])],"derivedFrom":subQ1}),-1.0]])]});}
            var Q52;
            {var subQ0=sQuery(id+"F0.wireOp",EDGE,"E48.8.0.1");var subQ1=sQuery(id+"F0.wireOp",EDGE,"E38.top");var subQ2=makeQuery(id+"F0.imprint","INTERSECT",VERTEX,{"derivedFrom":[subQ1,subQ0]});Q52=makeQuery(id+"F0.imprint","IMPRINT",FACE,{"disambiguationData":[TD([[makeQuery(id+"F0.imprint","IMPRINT",EDGE,{"disambiguationData":[TD([[subQ2,-1.0]])],"derivedFrom":subQ1}),1.0]])]});}
            var Q53;
            {var subQ0=sQuery(id+"F0.wireOp",EDGE,"E48.8.0.2");var subQ1=sQuery(id+"F0.wireOp",EDGE,"E38.top");var subQ2=makeQuery(id+"F0.imprint","INTERSECT",VERTEX,{"derivedFrom":[subQ1,subQ0]});Q53=makeQuery(id+"F0.imprint","IMPRINT",FACE,{"disambiguationData":[TD([[makeQuery(id+"F0.imprint","IMPRINT",EDGE,{"disambiguationData":[TD([[subQ2,-1.0]])],"derivedFrom":subQ1}),-1.0]])]});}
            var Q54;
            {var subQ0=sQuery(id+"F0.wireOp",EDGE,"E48.8.0.2");var subQ1=sQuery(id+"F0.wireOp",EDGE,"E38.top");var subQ2=makeQuery(id+"F0.imprint","INTERSECT",VERTEX,{"derivedFrom":[subQ1,subQ0]});Q54=makeQuery(id+"F0.imprint","IMPRINT",FACE,{"disambiguationData":[TD([[makeQuery(id+"F0.imprint","IMPRINT",EDGE,{"disambiguationData":[TD([[subQ2,-1.0]])],"derivedFrom":subQ1}),1.0]])]});}
            var Q55;
            {var subQ0=sQuery(id+"F0.wireOp",EDGE,"E48.8.0.0");var subQ3=sQuery(id+"F0.wireOp",EDGE,"E48.9.0.3");var subQ5=makeQuery(id+"F0.imprint","INTERSECT",VERTEX,{"derivedFrom":[subQ0,subQ3]});Q55=makeQuery(id+"F0.imprint","IMPRINT",FACE,{"disambiguationData":[TD([[makeQuery(id+"F0.imprint","IMPRINT",EDGE,{"disambiguationData":[TD([[subQ5,-1.0]])],"derivedFrom":subQ0}),1.0]])]});}
            var Q56;
            {var subQ5=sQuery(id+"F0.wireOp",EDGE,"E48.9.0.3");var subQ7=sQuery(id+"F0.wireOp",EDGE,"E38.top");var subQ9=makeQuery(id+"F0.imprint","INTERSECT",VERTEX,{"derivedFrom":[subQ7,subQ5]});Q56=makeQuery(id+"F0.imprint","IMPRINT",FACE,{"disambiguationData":[TD([[makeQuery(id+"F0.imprint","IMPRINT",EDGE,{"disambiguationData":[TD([[subQ9,-1.0]])],"derivedFrom":subQ7}),1.0]])]});}
            var Q57;
            {var subQ0=sQuery(id+"F0.wireOp",EDGE,"E48.9.0.3");var subQ1=sQuery(id+"F0.wireOp",EDGE,"E38.top");var subQ2=makeQuery(id+"F0.imprint","INTERSECT",VERTEX,{"derivedFrom":[subQ1,subQ0]});Q57=makeQuery(id+"F0.imprint","IMPRINT",FACE,{"disambiguationData":[TD([[makeQuery(id+"F0.imprint","IMPRINT",EDGE,{"disambiguationData":[TD([[subQ2,-1.0]])],"derivedFrom":subQ1}),-1.0]])]});}
            var Q58;
            {var subQ0=sQuery(id+"F0.wireOp",EDGE,"E48.9.0.1");var subQ1=sQuery(id+"F0.wireOp",EDGE,"E38.top");var subQ2=makeQuery(id+"F0.imprint","INTERSECT",VERTEX,{"derivedFrom":[subQ1,subQ0]});Q58=makeQuery(id+"F0.imprint","IMPRINT",FACE,{"disambiguationData":[TD([[makeQuery(id+"F0.imprint","IMPRINT",EDGE,{"disambiguationData":[TD([[subQ2,-1.0]])],"derivedFrom":subQ1}),1.0]])]});}
            var Q59;
            {var subQ0=sQuery(id+"F0.wireOp",EDGE,"E48.9.0.2");var subQ1=sQuery(id+"F0.wireOp",EDGE,"E38.top");var subQ2=makeQuery(id+"F0.imprint","INTERSECT",VERTEX,{"derivedFrom":[subQ1,subQ0]});Q59=makeQuery(id+"F0.imprint","IMPRINT",FACE,{"disambiguationData":[TD([[makeQuery(id+"F0.imprint","IMPRINT",EDGE,{"disambiguationData":[TD([[subQ2,-1.0]])],"derivedFrom":subQ1}),1.0]])]});}
            var Q60;
            {var subQ0=sQuery(id+"F0.wireOp",EDGE,"E48.9.0.2");var subQ1=sQuery(id+"F0.wireOp",EDGE,"E38.top");var subQ2=makeQuery(id+"F0.imprint","INTERSECT",VERTEX,{"derivedFrom":[subQ1,subQ0]});Q60=makeQuery(id+"F0.imprint","IMPRINT",FACE,{"disambiguationData":[TD([[makeQuery(id+"F0.imprint","IMPRINT",EDGE,{"disambiguationData":[TD([[subQ2,-1.0]])],"derivedFrom":subQ1}),-1.0]])]});}
            var Q61;
            {var subQ0=sQuery(id+"F0.wireOp",EDGE,"E48.9.0.0");var subQ3=sQuery(id+"F0.wireOp",EDGE,"E48.10.0.3");var subQ5=makeQuery(id+"F0.imprint","INTERSECT",VERTEX,{"derivedFrom":[subQ0,subQ3]});Q61=makeQuery(id+"F0.imprint","IMPRINT",FACE,{"disambiguationData":[TD([[makeQuery(id+"F0.imprint","IMPRINT",EDGE,{"disambiguationData":[TD([[subQ5,-1.0]])],"derivedFrom":subQ0}),1.0]])]});}
            var Q62;
            {var subQ5=sQuery(id+"F0.wireOp",EDGE,"E38.top");var subQ7=sQuery(id+"F0.wireOp",EDGE,"E48.10.0.3");var subQ9=makeQuery(id+"F0.imprint","INTERSECT",VERTEX,{"derivedFrom":[subQ5,subQ7]});Q62=makeQuery(id+"F0.imprint","IMPRINT",FACE,{"disambiguationData":[TD([[makeQuery(id+"F0.imprint","IMPRINT",EDGE,{"disambiguationData":[TD([[subQ9,-1.0]])],"derivedFrom":subQ5}),1.0]])]});}
            var Q63;
            {var subQ0=sQuery(id+"F0.wireOp",EDGE,"E48.10.0.3");var subQ1=sQuery(id+"F0.wireOp",EDGE,"E38.top");var subQ2=makeQuery(id+"F0.imprint","INTERSECT",VERTEX,{"derivedFrom":[subQ1,subQ0]});Q63=makeQuery(id+"F0.imprint","IMPRINT",FACE,{"disambiguationData":[TD([[makeQuery(id+"F0.imprint","IMPRINT",EDGE,{"disambiguationData":[TD([[subQ2,-1.0]])],"derivedFrom":subQ1}),-1.0]])]});}
            var Q64;
            {var subQ0=sQuery(id+"F0.wireOp",EDGE,"E48.10.0.1");var subQ1=sQuery(id+"F0.wireOp",EDGE,"E38.top");var subQ2=makeQuery(id+"F0.imprint","INTERSECT",VERTEX,{"derivedFrom":[subQ1,subQ0]});Q64=makeQuery(id+"F0.imprint","IMPRINT",FACE,{"disambiguationData":[TD([[makeQuery(id+"F0.imprint","IMPRINT",EDGE,{"disambiguationData":[TD([[subQ2,-1.0]])],"derivedFrom":subQ1}),1.0]])]});}
            var Q65;
            {var subQ0=sQuery(id+"F0.wireOp",EDGE,"E48.10.0.2");var subQ1=sQuery(id+"F0.wireOp",EDGE,"E38.top");var subQ2=makeQuery(id+"F0.imprint","INTERSECT",VERTEX,{"derivedFrom":[subQ1,subQ0]});Q65=makeQuery(id+"F0.imprint","IMPRINT",FACE,{"disambiguationData":[TD([[makeQuery(id+"F0.imprint","IMPRINT",EDGE,{"disambiguationData":[TD([[subQ2,-1.0]])],"derivedFrom":subQ1}),-1.0]])]});}
            var Q66;
            {var subQ0=sQuery(id+"F0.wireOp",EDGE,"E48.10.0.2");var subQ1=sQuery(id+"F0.wireOp",EDGE,"E38.top");var subQ2=makeQuery(id+"F0.imprint","INTERSECT",VERTEX,{"derivedFrom":[subQ1,subQ0]});Q66=makeQuery(id+"F0.imprint","IMPRINT",FACE,{"disambiguationData":[TD([[makeQuery(id+"F0.imprint","IMPRINT",EDGE,{"disambiguationData":[TD([[subQ2,-1.0]])],"derivedFrom":subQ1}),1.0]])]});}
            var Q67;
            {var subQ0=sQuery(id+"F0.wireOp",EDGE,"E48.10.0.0");var subQ3=sQuery(id+"F0.wireOp",EDGE,"E48.11.0.3");var subQ5=makeQuery(id+"F0.imprint","INTERSECT",VERTEX,{"derivedFrom":[subQ0,subQ3]});Q67=makeQuery(id+"F0.imprint","IMPRINT",FACE,{"disambiguationData":[TD([[makeQuery(id+"F0.imprint","IMPRINT",EDGE,{"disambiguationData":[TD([[subQ5,-1.0]])],"derivedFrom":subQ0}),1.0]])]});}
            var Q68;
            {var subQ0=sQuery(id+"F0.wireOp",EDGE,"E48.11.0.3");var subQ1=sQuery(id+"F0.wireOp",EDGE,"E38.top");var subQ2=makeQuery(id+"F0.imprint","INTERSECT",VERTEX,{"derivedFrom":[subQ1,subQ0]});Q68=makeQuery(id+"F0.imprint","IMPRINT",FACE,{"disambiguationData":[TD([[makeQuery(id+"F0.imprint","IMPRINT",EDGE,{"disambiguationData":[TD([[subQ2,-1.0]])],"derivedFrom":subQ1}),-1.0]])]});}
            var Q69;
            {var subQ0=sQuery(id+"F0.wireOp",EDGE,"E48.11.0.1");var subQ1=sQuery(id+"F0.wireOp",EDGE,"E38.top");var subQ2=makeQuery(id+"F0.imprint","INTERSECT",VERTEX,{"derivedFrom":[subQ1,subQ0]});Q69=makeQuery(id+"F0.imprint","IMPRINT",FACE,{"disambiguationData":[TD([[makeQuery(id+"F0.imprint","IMPRINT",EDGE,{"disambiguationData":[TD([[subQ2,-1.0]])],"derivedFrom":subQ1}),1.0]])]});}
            var Q70;
            {var subQ0=sQuery(id+"F0.wireOp",EDGE,"E48.11.0.2");var subQ1=sQuery(id+"F0.wireOp",EDGE,"E38.top");var subQ2=makeQuery(id+"F0.imprint","INTERSECT",VERTEX,{"derivedFrom":[subQ1,subQ0]});Q70=makeQuery(id+"F0.imprint","IMPRINT",FACE,{"disambiguationData":[TD([[makeQuery(id+"F0.imprint","IMPRINT",EDGE,{"disambiguationData":[TD([[subQ2,-1.0]])],"derivedFrom":subQ1}),-1.0]])]});}
            var Q71;
            {var subQ0=sQuery(id+"F0.wireOp",EDGE,"E48.11.0.2");var subQ1=sQuery(id+"F0.wireOp",EDGE,"E38.top");var subQ2=makeQuery(id+"F0.imprint","INTERSECT",VERTEX,{"derivedFrom":[subQ1,subQ0]});Q71=makeQuery(id+"F0.imprint","IMPRINT",FACE,{"disambiguationData":[TD([[makeQuery(id+"F0.imprint","IMPRINT",EDGE,{"disambiguationData":[TD([[subQ2,-1.0]])],"derivedFrom":subQ1}),1.0]])]});}
            var Q72;
            {var subQ0=sQuery(id+"F0.wireOp",EDGE,"E48.11.0.0");var subQ3=sQuery(id+"F0.wireOp",EDGE,"E48.12.0.3");var subQ5=makeQuery(id+"F0.imprint","INTERSECT",VERTEX,{"derivedFrom":[subQ0,subQ3]});Q72=makeQuery(id+"F0.imprint","IMPRINT",FACE,{"disambiguationData":[TD([[makeQuery(id+"F0.imprint","IMPRINT",EDGE,{"disambiguationData":[TD([[subQ5,-1.0]])],"derivedFrom":subQ0}),1.0]])]});}
            var Q73;
            {var subQ0=sQuery(id+"F0.wireOp",EDGE,"E48.12.0.3");var subQ1=sQuery(id+"F0.wireOp",EDGE,"E38.top");var subQ2=makeQuery(id+"F0.imprint","INTERSECT",VERTEX,{"derivedFrom":[subQ1,subQ0]});Q73=makeQuery(id+"F0.imprint","IMPRINT",FACE,{"disambiguationData":[TD([[makeQuery(id+"F0.imprint","IMPRINT",EDGE,{"disambiguationData":[TD([[subQ2,-1.0]])],"derivedFrom":subQ1}),-1.0]])]});}
            var Q74;
            {var subQ1=sQuery(id+"F0.wireOp",EDGE,"E38.top");var subQ7=sQuery(id+"F0.wireOp",EDGE,"E48.12.0.3");var subQ9=makeQuery(id+"F0.imprint","INTERSECT",VERTEX,{"derivedFrom":[subQ1,subQ7]});Q74=makeQuery(id+"F0.imprint","IMPRINT",FACE,{"disambiguationData":[TD([[makeQuery(id+"F0.imprint","IMPRINT",EDGE,{"disambiguationData":[TD([[subQ9,-1.0]])],"derivedFrom":subQ1}),1.0]])]});}
            var Q75;
            {var subQ0=sQuery(id+"F0.wireOp",EDGE,"E48.12.0.1");var subQ1=sQuery(id+"F0.wireOp",EDGE,"E38.top");var subQ2=makeQuery(id+"F0.imprint","INTERSECT",VERTEX,{"derivedFrom":[subQ1,subQ0]});Q75=makeQuery(id+"F0.imprint","IMPRINT",FACE,{"disambiguationData":[TD([[makeQuery(id+"F0.imprint","IMPRINT",EDGE,{"disambiguationData":[TD([[subQ2,-1.0]])],"derivedFrom":subQ1}),1.0]])]});}
            var Q76;
            {var subQ0=sQuery(id+"F0.wireOp",EDGE,"E48.12.0.2");var subQ1=sQuery(id+"F0.wireOp",EDGE,"E38.top");var subQ2=makeQuery(id+"F0.imprint","INTERSECT",VERTEX,{"derivedFrom":[subQ1,subQ0]});Q76=makeQuery(id+"F0.imprint","IMPRINT",FACE,{"disambiguationData":[TD([[makeQuery(id+"F0.imprint","IMPRINT",EDGE,{"disambiguationData":[TD([[subQ2,-1.0]])],"derivedFrom":subQ1}),-1.0]])]});}
            var Q77;
            {var subQ3=sQuery(id+"F0.wireOp",EDGE,"E48.12.0.2");var subQ6=sQuery(id+"F0.wireOp",EDGE,"E38.top");var subQ9=makeQuery(id+"F0.imprint","INTERSECT",VERTEX,{"derivedFrom":[subQ6,subQ3]});Q77=makeQuery(id+"F0.imprint","IMPRINT",FACE,{"disambiguationData":[TD([[makeQuery(id+"F0.imprint","IMPRINT",EDGE,{"disambiguationData":[TD([[subQ9,-1.0]])],"derivedFrom":subQ6}),1.0]])]});}
            var Q78;
            {var subQ5=sQuery(id+"F0.wireOp",EDGE,"E48.13.0.3");var subQ6=sQuery(id+"F0.wireOp",EDGE,"E38.top");var subQ7=makeQuery(id+"F0.imprint","INTERSECT",VERTEX,{"derivedFrom":[subQ6,subQ5]});Q78=makeQuery(id+"F0.imprint","IMPRINT",FACE,{"disambiguationData":[TD([[makeQuery(id+"F0.imprint","IMPRINT",EDGE,{"disambiguationData":[TD([[subQ7,-1.0]])],"derivedFrom":subQ6}),1.0]])]});}
            var Q79;
            {var subQ0=sQuery(id+"F0.wireOp",EDGE,"E48.13.0.3");var subQ1=sQuery(id+"F0.wireOp",EDGE,"E38.top");var subQ2=makeQuery(id+"F0.imprint","INTERSECT",VERTEX,{"derivedFrom":[subQ1,subQ0]});Q79=makeQuery(id+"F0.imprint","IMPRINT",FACE,{"disambiguationData":[TD([[makeQuery(id+"F0.imprint","IMPRINT",EDGE,{"disambiguationData":[TD([[subQ2,-1.0]])],"derivedFrom":subQ1}),-1.0]])]});}
            var Q80;
            {var subQ0=sQuery(id+"F0.wireOp",EDGE,"E48.13.0.2");var subQ1=sQuery(id+"F0.wireOp",EDGE,"E38.top");var subQ2=makeQuery(id+"F0.imprint","INTERSECT",VERTEX,{"derivedFrom":[subQ1,subQ0]});Q80=makeQuery(id+"F0.imprint","IMPRINT",FACE,{"disambiguationData":[TD([[makeQuery(id+"F0.imprint","IMPRINT",EDGE,{"disambiguationData":[TD([[subQ2,-1.0]])],"derivedFrom":subQ1}),-1.0]])]});}
            var Q81;
            {var subQ1=sQuery(id+"F0.wireOp",EDGE,"E38.top");var subQ7=sQuery(id+"F0.wireOp",EDGE,"E48.13.0.2");var subQ9=makeQuery(id+"F0.imprint","INTERSECT",VERTEX,{"derivedFrom":[subQ1,subQ7]});Q81=makeQuery(id+"F0.imprint","IMPRINT",FACE,{"disambiguationData":[TD([[makeQuery(id+"F0.imprint","IMPRINT",EDGE,{"disambiguationData":[TD([[subQ9,-1.0]])],"derivedFrom":subQ1}),1.0]])]});}
            var Q82;
            {var subQ0=sQuery(id+"F0.wireOp",EDGE,"E48.13.0.1");var subQ1=sQuery(id+"F0.wireOp",EDGE,"E38.top");var subQ2=makeQuery(id+"F0.imprint","INTERSECT",VERTEX,{"derivedFrom":[subQ1,subQ0]});Q82=makeQuery(id+"F0.imprint","IMPRINT",FACE,{"disambiguationData":[TD([[makeQuery(id+"F0.imprint","IMPRINT",EDGE,{"disambiguationData":[TD([[subQ2,-1.0]])],"derivedFrom":subQ1}),1.0]])]});}
            var Q83;
            {var subQ5=sQuery(id+"F0.wireOp",EDGE,"E48.14.0.3");var subQ7=sQuery(id+"F0.wireOp",EDGE,"E38.top");var subQ8=makeQuery(id+"F0.imprint","INTERSECT",VERTEX,{"derivedFrom":[subQ7,subQ5]});Q83=makeQuery(id+"F0.imprint","IMPRINT",FACE,{"disambiguationData":[TD([[makeQuery(id+"F0.imprint","IMPRINT",EDGE,{"disambiguationData":[TD([[subQ8,-1.0]])],"derivedFrom":subQ7}),1.0]])]});}
            var Q84;
            {var subQ0=sQuery(id+"F0.wireOp",EDGE,"E48.14.0.3");var subQ1=sQuery(id+"F0.wireOp",EDGE,"E38.top");var subQ2=makeQuery(id+"F0.imprint","INTERSECT",VERTEX,{"derivedFrom":[subQ1,subQ0]});Q84=makeQuery(id+"F0.imprint","IMPRINT",FACE,{"disambiguationData":[TD([[makeQuery(id+"F0.imprint","IMPRINT",EDGE,{"disambiguationData":[TD([[subQ2,-1.0]])],"derivedFrom":subQ1}),-1.0]])]});}
            var Q85;
            {var subQ0=sQuery(id+"F0.wireOp",EDGE,"E48.14.0.1");var subQ1=sQuery(id+"F0.wireOp",EDGE,"E38.top");var subQ2=makeQuery(id+"F0.imprint","INTERSECT",VERTEX,{"derivedFrom":[subQ1,subQ0]});Q85=makeQuery(id+"F0.imprint","IMPRINT",FACE,{"disambiguationData":[TD([[makeQuery(id+"F0.imprint","IMPRINT",EDGE,{"disambiguationData":[TD([[subQ2,-1.0]])],"derivedFrom":subQ1}),1.0]])]});}
            var Q86;
            {var subQ5=sQuery(id+"F0.wireOp",EDGE,"E48.14.0.2");var subQ6=sQuery(id+"F0.wireOp",EDGE,"E38.top");var subQ7=makeQuery(id+"F0.imprint","INTERSECT",VERTEX,{"derivedFrom":[subQ6,subQ5]});Q86=makeQuery(id+"F0.imprint","IMPRINT",FACE,{"disambiguationData":[TD([[makeQuery(id+"F0.imprint","IMPRINT",EDGE,{"disambiguationData":[TD([[subQ7,-1.0]])],"derivedFrom":subQ6}),1.0]])]});}
            var Q87;
            {var subQ0=sQuery(id+"F0.wireOp",EDGE,"E48.14.0.2");var subQ1=sQuery(id+"F0.wireOp",EDGE,"E38.top");var subQ2=makeQuery(id+"F0.imprint","INTERSECT",VERTEX,{"derivedFrom":[subQ1,subQ0]});Q87=makeQuery(id+"F0.imprint","IMPRINT",FACE,{"disambiguationData":[TD([[makeQuery(id+"F0.imprint","IMPRINT",EDGE,{"disambiguationData":[TD([[subQ2,-1.0]])],"derivedFrom":subQ1}),-1.0]])]});}
            var Q88;
            Q88=makeQuery(id+"F0.imprint","IMPRINT",FACE,{"disambiguationData":[TD([[makeQuery(id+"F0.imprint","IMPRINT",EDGE,{"derivedFrom":sQuery(id+"F0.wireOp",EDGE,"E0.bottom")}),-1.0]])]});
            var Q89;
            {var subQ1=sQuery(id+"F0.wireOp",EDGE,"E38.top");var subQ5=sQuery(id+"F0.wireOp",EDGE,"E48.11.0.3");var subQ6=makeQuery(id+"F0.imprint","INTERSECT",VERTEX,{"derivedFrom":[subQ1,subQ5]});Q89=makeQuery(id+"F0.imprint","IMPRINT",FACE,{"disambiguationData":[TD([[makeQuery(id+"F0.imprint","IMPRINT",EDGE,{"disambiguationData":[TD([[subQ6,-1.0]])],"derivedFrom":subQ1}),1.0]])]});}
            extrude(context, id + "F6", {"entities" : qUnion([Q0, Q1, Q2, Q3, Q4, Q5, Q6, Q7, Q8, Q9, Q10, Q11, Q12, Q13, Q14, Q15, Q16, Q17, Q18, Q19, Q20, Q21, Q22, Q23, Q24, Q25, Q26, Q27, Q28, Q29, Q30, Q31, Q32, Q33, Q34, Q35, Q36, Q37, Q38, Q39, Q40, Q41, Q42, Q43, Q44, Q45, Q46, Q47, Q48, Q49, Q50, Q51, Q52, Q53, Q54, Q55, Q56, Q57, Q58, Q59, Q60, Q61, Q62, Q63, Q64, Q65, Q66, Q67, Q68, Q69, Q70, Q71, Q72, Q73, Q74, Q75, Q76, Q77, Q78, Q79, Q80, Q81, Q82, Q83, Q84, Q85, Q86, Q87, Q88, Q89]), "operationType" : NewBodyOperationType.ADD, "depth" : 1 / 101.6 * mm});
        }
        {
            var Q0;
            {var subQ0=sQuery(id+"F0.wireOp",EDGE,"E39");var subQ1=sQuery(id+"F0.wireOp",EDGE,"E38.right");var subQ2=sQuery(id+"F0.wireOp",EDGE,"E38.left");var subQ3=sQuery(id+"F0.wireOp",EDGE,"E38.top");var subQ4=sQuery(id+"F0.wireOp",EDGE,"E38.bottom");var subQ5=sQuery(id+"F0.wireOp",EDGE,"E0.right");var subQ6=sQuery(id+"F0.wireOp",EDGE,"E0.left");var subQ7=sQuery(id+"F0.wireOp",EDGE,"E0.top");Q0=makeQuery(id+"F6.boolean.opBoolean","MERGE",FACE,{"derivedFrom":[makeQuery(id+"F3.boolean.opBoolean","MERGE",FACE,{"derivedFrom":[makeQuery(id+"F1.opExtrude","CAP_FACE",FACE,{"disambiguationData":[OSD([subQ7,subQ6,subQ5,sQuery(id+"F0.wireOp",EDGE,"E1"),sQuery(id+"F0.wireOp",EDGE,"E2"),sQuery(id+"F0.wireOp",EDGE,"E3"),sQuery(id+"F0.wireOp",EDGE,"E4"),sQuery(id+"F0.wireOp",EDGE,"E5"),sQuery(id+"F0.wireOp",EDGE,"E6"),sQuery(id+"F0.wireOp",EDGE,"E7"),sQuery(id+"F0.wireOp",EDGE,"E8"),sQuery(id+"F0.wireOp",EDGE,"E9"),sQuery(id+"F0.wireOp",EDGE,"E10"),sQuery(id+"F0.wireOp",EDGE,"E11"),sQuery(id+"F0.wireOp",EDGE,"E12"),sQuery(id+"F0.wireOp",EDGE,"E13"),sQuery(id+"F0.wireOp",EDGE,"E14"),sQuery(id+"F0.wireOp",EDGE,"E15"),sQuery(id+"F0.wireOp",EDGE,"E16"),sQuery(id+"F0.wireOp",EDGE,"E17"),sQuery(id+"F0.wireOp",EDGE,"E18"),sQuery(id+"F0.wireOp",EDGE,"E19"),sQuery(id+"F0.wireOp",EDGE,"E20"),sQuery(id+"F0.wireOp",EDGE,"E21"),sQuery(id+"F0.wireOp",EDGE,"E22"),sQuery(id+"F0.wireOp",EDGE,"E23"),sQuery(id+"F0.wireOp",EDGE,"E24"),sQuery(id+"F0.wireOp",EDGE,"E25"),sQuery(id+"F0.wireOp",EDGE,"E26"),sQuery(id+"F0.wireOp",EDGE,"E27"),sQuery(id+"F0.wireOp",EDGE,"E28"),sQuery(id+"F0.wireOp",EDGE,"E29"),sQuery(id+"F0.wireOp",EDGE,"E30"),sQuery(id+"F0.wireOp",EDGE,"E31"),sQuery(id+"F0.wireOp",EDGE,"E32"),sQuery(id+"F0.wireOp",EDGE,"E33"),sQuery(id+"F0.wireOp",EDGE,"E34"),sQuery(id+"F0.wireOp",EDGE,"E35"),subQ4,subQ3,subQ2,subQ1,subQ0])],"isStart":false}),makeQuery(id+"F3.opExtrude","SWEPT_FACE",FACE,{"disambiguationData":[OSD([sQuery(id+"F2.wireOp",EDGE,"E49.top")])]}),makeQuery(id+"F3.opExtrude","SWEPT_FACE",FACE,{"disambiguationData":[OSD([sQuery(id+"F2.wireOp",EDGE,"E50.1.0.3")])]}),makeQuery(id+"F3.opExtrude","SWEPT_FACE",FACE,{"disambiguationData":[OSD([sQuery(id+"F2.wireOp",EDGE,"E50.2.0.3")])]}),makeQuery(id+"F3.opExtrude","SWEPT_FACE",FACE,{"disambiguationData":[OSD([sQuery(id+"F2.wireOp",EDGE,"E50.3.0.3")])]}),makeQuery(id+"F3.opExtrude","SWEPT_FACE",FACE,{"disambiguationData":[OSD([sQuery(id+"F2.wireOp",EDGE,"E50.4.0.3")])]}),makeQuery(id+"F3.opExtrude","SWEPT_FACE",FACE,{"disambiguationData":[OSD([sQuery(id+"F2.wireOp",EDGE,"E50.5.0.3")])]}),makeQuery(id+"F3.opExtrude","SWEPT_FACE",FACE,{"disambiguationData":[OSD([sQuery(id+"F2.wireOp",EDGE,"E50.6.0.3")])]})]}),makeQuery(id+"F6.opExtrude","CAP_FACE",FACE,{"disambiguationData":[OSD([sQuery(id+"F0.wireOp",EDGE,"E0.bottom"),subQ7,subQ6,subQ5,subQ4,subQ3,subQ2,subQ1,subQ0,sQuery(id+"F0.wireOp",EDGE,"E42"),sQuery(id+"F0.wireOp",EDGE,"E43"),sQuery(id+"F0.wireOp",EDGE,"E44"),sQuery(id+"F0.wireOp",EDGE,"E45"),sQuery(id+"F0.wireOp",EDGE,"E46"),sQuery(id+"F0.wireOp",EDGE,"E47"),sQuery(id+"F0.wireOp",EDGE,"E48.1.0.0"),sQuery(id+"F0.wireOp",EDGE,"E48.1.0.1"),sQuery(id+"F0.wireOp",EDGE,"E48.1.0.2"),sQuery(id+"F0.wireOp",EDGE,"E48.1.0.3"),sQuery(id+"F0.wireOp",EDGE,"E48.2.0.0"),sQuery(id+"F0.wireOp",EDGE,"E48.2.0.1"),sQuery(id+"F0.wireOp",EDGE,"E48.2.0.2"),sQuery(id+"F0.wireOp",EDGE,"E48.2.0.3"),sQuery(id+"F0.wireOp",EDGE,"E48.3.0.0"),sQuery(id+"F0.wireOp",EDGE,"E48.3.0.1"),sQuery(id+"F0.wireOp",EDGE,"E48.3.0.2"),sQuery(id+"F0.wireOp",EDGE,"E48.3.0.3"),sQuery(id+"F0.wireOp",EDGE,"E48.4.0.0"),sQuery(id+"F0.wireOp",EDGE,"E48.4.0.1"),sQuery(id+"F0.wireOp",EDGE,"E48.4.0.2"),sQuery(id+"F0.wireOp",EDGE,"E48.4.0.3"),sQuery(id+"F0.wireOp",EDGE,"E48.5.0.0"),sQuery(id+"F0.wireOp",EDGE,"E48.5.0.1"),sQuery(id+"F0.wireOp",EDGE,"E48.5.0.2"),sQuery(id+"F0.wireOp",EDGE,"E48.5.0.3"),sQuery(id+"F0.wireOp",EDGE,"E48.6.0.0"),sQuery(id+"F0.wireOp",EDGE,"E48.6.0.1"),sQuery(id+"F0.wireOp",EDGE,"E48.6.0.2"),sQuery(id+"F0.wireOp",EDGE,"E48.6.0.3"),sQuery(id+"F0.wireOp",EDGE,"E48.7.0.0"),sQuery(id+"F0.wireOp",EDGE,"E48.7.0.1"),sQuery(id+"F0.wireOp",EDGE,"E48.7.0.2"),sQuery(id+"F0.wireOp",EDGE,"E48.7.0.3"),sQuery(id+"F0.wireOp",EDGE,"E48.8.0.0"),sQuery(id+"F0.wireOp",EDGE,"E48.8.0.1"),sQuery(id+"F0.wireOp",EDGE,"E48.8.0.2"),sQuery(id+"F0.wireOp",EDGE,"E48.8.0.3"),sQuery(id+"F0.wireOp",EDGE,"E48.9.0.0"),sQuery(id+"F0.wireOp",EDGE,"E48.9.0.1"),sQuery(id+"F0.wireOp",EDGE,"E48.9.0.2"),sQuery(id+"F0.wireOp",EDGE,"E48.9.0.3"),sQuery(id+"F0.wireOp",EDGE,"E48.10.0.0"),sQuery(id+"F0.wireOp",EDGE,"E48.10.0.1"),sQuery(id+"F0.wireOp",EDGE,"E48.10.0.2"),sQuery(id+"F0.wireOp",EDGE,"E48.10.0.3"),sQuery(id+"F0.wireOp",EDGE,"E48.11.0.0"),sQuery(id+"F0.wireOp",EDGE,"E48.11.0.1"),sQuery(id+"F0.wireOp",EDGE,"E48.12.0.0"),sQuery(id+"F0.wireOp",EDGE,"E48.12.0.1"),sQuery(id+"F0.wireOp",EDGE,"E48.12.0.2"),sQuery(id+"F0.wireOp",EDGE,"E48.12.0.3"),sQuery(id+"F0.wireOp",EDGE,"E48.13.0.0"),sQuery(id+"F0.wireOp",EDGE,"E48.13.0.1"),sQuery(id+"F0.wireOp",EDGE,"E48.13.0.2"),sQuery(id+"F0.wireOp",EDGE,"E48.13.0.3"),sQuery(id+"F0.wireOp",EDGE,"E48.14.0.0"),sQuery(id+"F0.wireOp",EDGE,"E48.14.0.1"),sQuery(id+"F0.wireOp",EDGE,"E48.14.0.2"),sQuery(id+"F0.wireOp",EDGE,"E48.14.0.3")])],"isStart":false})]});}
            var sketch = newSketch(context, id + "F7", { "sketchPlane" : qUnion([Q0])});
            skPoint(sketch, "E52", {"position": v(69.15, 6.9) * mm});
            skLineSegment(sketch, "E53", {"start": v(92.4, 9.2) * mm, "end": v(92.4, 20) * mm});
            skLineSegment(sketch, "E54", {"start": v(92.4, 20) * mm, "end": v(98.75, 20) * mm});
            skLineSegment(sketch, "E55", {"start": v(98.75, 20) * mm, "end": v(98.75, 7.5) * mm});
            skLineSegment(sketch, "E56", {"start": v(43.75, 20) * mm, "end": v(43.75, 16.27) * mm});
            skLineSegment(sketch, "E57", {"start": v(43.75, 16.27) * mm, "end": v(92.4, 16.27) * mm});
            skPoint(sketch, "E57.endSnap0", {"position": v(92.4, 14.6) * mm});
            skLineSegment(sketch, "E58", {"start": v(43.75, 20) * mm, "end": v(53.3, 20) * mm});
            skLineSegment(sketch, "E59", {"start": v(53.3, 20) * mm, "end": v(53.3, 16.27) * mm});
            skLineSegment(sketch, "E60", {"start": v(-98.75, -5) * mm, "end": v(-122.13, -5) * mm});
            skFitSpline(sketch, "E61", {"points": [v(-122.13, -5) * mm, v(-67.75, -14.32) * mm], "startDerivative": vector(8.04, -21.79) * mm, "endDerivative": vector(94.74, -17.55) * mm});
            skSolve(sketch);
        }
        {
            var Q0;
            {var subQ7=sQuery(id+"F7.wireOp",EDGE,"E59");Q0=makeQuery(id+"F7.imprint","IMPRINT",FACE,{"disambiguationData":[TD([[makeQuery(id+"F7.imprint","IMPRINT",EDGE,{"derivedFrom":subQ7}),1.0]])]});}
            extrude(context, id + "F8", {"entities" : qUnion([Q0]), "operationType" : NewBodyOperationType.REMOVE, "oppositeDirection" : true, "depth" : 25 * mm});
        }
        {
            var Q0;
            {var subQ0=sQuery(id+"F7.wireOp",EDGE,"E60");Q0=makeQuery(id+"F7.imprint","IMPRINT",FACE,{"disambiguationData":[TD([[makeQuery(id+"F7.imprint","IMPRINT",EDGE,{"derivedFrom":subQ0}),1.0]])]});}
            extrude(context, id + "F9", {"entities" : qUnion([Q0]), "operationType" : NewBodyOperationType.ADD, "oppositeDirection" : true, "depth" : 6.35 * mm});
        }
        {
            var Q0;
            Q0=makeQuery(id+"F5.imprint","IMPRINT",FACE,{"disambiguationData":[TD([[makeQuery(id+"F5.imprint","IMPRINT",EDGE,{"derivedFrom":sQuery(id+"F5.wireOp",EDGE,"E51.bottom")}),-1.0]])]});
            extrude(context, id + "F10", {"entities" : qUnion([Q0]), "operationType" : NewBodyOperationType.REMOVE, "oppositeDirection" : true, "depth" : 25 * mm});
        }
    });
